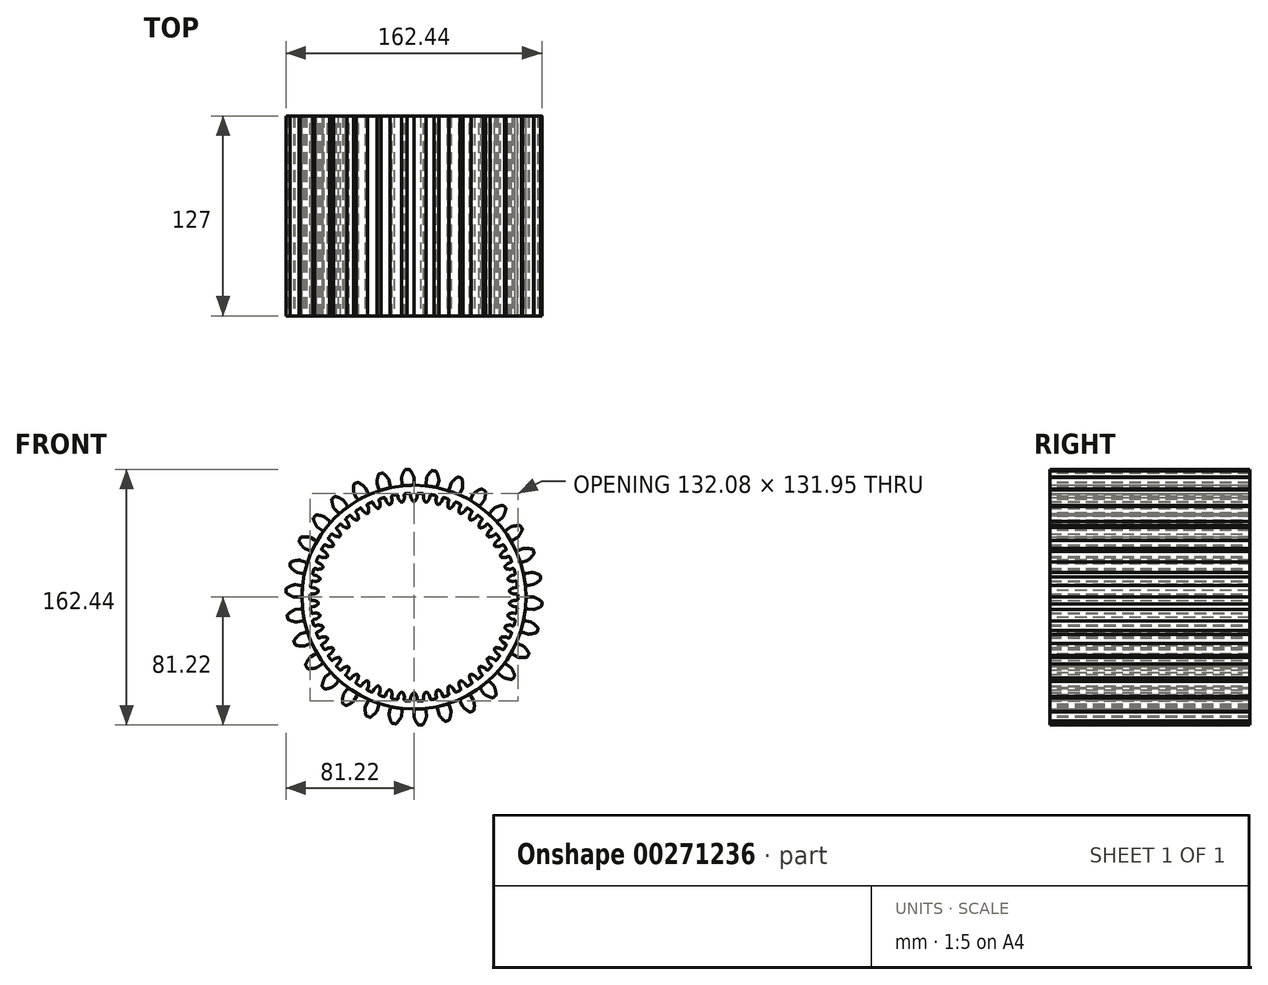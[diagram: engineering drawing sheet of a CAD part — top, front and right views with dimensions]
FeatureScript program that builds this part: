
annotation { "Feature Type Name" : "Feature", "Feature Type Description" : "" }
export const myFeature = defineFeature(function(context is Context, id is Id, definition is map)
    precondition{}
    {
        {
            var Q0;
            Q0=qCreatedBy(makeId("Front.planeOp"),FACE);
            var sketch = newSketch(context, id + "F0", { "sketchPlane" : qUnion([Q0])});
            skArc(sketch, "E0", {"start": v(-2.9, 65.98) * mm, "mid": v(-4.15, 65.9) * mm, "end": v(-5.38, 65.82) * mm});
            skArc(sketch, "E1.MirrorCS", {"start": v(1.94, 63.33) * mm, "mid": v(1.43, 62.22) * mm, "end": v(0.84, 61.15) * mm});
            skLineSegment(sketch, "E2", {"start": v(2, 63.62) * mm, "end": v(2.05, 65.18) * mm});
            skLineSegment(sketch, "E3", {"start": v(0.4, 60.9) * mm, "end": v(0, 60.9) * mm});
            skLineSegment(sketch, "E4.MirrorCS", {"start": v(-2, 63.62) * mm, "end": v(-2.05, 65.18) * mm});
            skArc(sketch, "E5.MirrorCS", {"start": v(-1.94, 63.33) * mm, "mid": v(-1.43, 62.22) * mm, "end": v(-0.84, 61.15) * mm});
            skLineSegment(sketch, "E6.MirrorCS", {"start": v(-0.4, 60.9) * mm, "end": v(0, 60.9) * mm});
            skPoint(sketch, "E7.visualSharp", {"position": v(2, 63.47) * mm});
            skArc(sketch, "E7.filletArc", {"start": v(1.94, 63.33) * mm, "mid": v(1.98, 63.47) * mm, "end": v(2, 63.62) * mm});
            skPoint(sketch, "E8.visualSharp", {"position": v(-2, 63.47) * mm});
            skArc(sketch, "E8.filletArc", {"start": v(-2, 63.62) * mm, "mid": v(-1.98, 63.47) * mm, "end": v(-1.94, 63.33) * mm});
            skPoint(sketch, "E9.visualSharp", {"position": v(-2.07, 66) * mm});
            skArc(sketch, "E9.filletArc", {"start": v(-2.05, 65.18) * mm, "mid": v(-2.31, 65.76) * mm, "end": v(-2.9, 65.98) * mm});
            skPoint(sketch, "E10.visualSharp", {"position": v(2.07, 66) * mm});
            skArc(sketch, "E10.filletArc", {"start": v(2.9, 65.98) * mm, "mid": v(2.31, 65.76) * mm, "end": v(2.05, 65.18) * mm});
            skPoint(sketch, "E11.visualSharp", {"position": v(-0.68, 60.9) * mm});
            skArc(sketch, "E11.filletArc", {"start": v(-0.84, 61.15) * mm, "mid": v(-0.65, 60.97) * mm, "end": v(-0.4, 60.9) * mm});
            skPoint(sketch, "E12.visualSharp", {"position": v(0.68, 60.9) * mm});
            skArc(sketch, "E12.filletArc", {"start": v(0.4, 60.9) * mm, "mid": v(0.65, 60.97) * mm, "end": v(0.84, 61.15) * mm});
            skArc(sketch, "E13.1.0", {"start": v(-5.38, 65.82) * mm, "mid": v(-5.95, 65.53) * mm, "end": v(-6.14, 64.92) * mm});
            skLineSegment(sketch, "E13.1.1", {"start": v(-5.99, 63.37) * mm, "end": v(-6.14, 64.92) * mm});
            skArc(sketch, "E13.1.2", {"start": v(-6.01, 63.07) * mm, "mid": v(-5.99, 63.22) * mm, "end": v(-5.99, 63.37) * mm});
            skArc(sketch, "E13.1.3", {"start": v(-6.01, 63.07) * mm, "mid": v(-6.38, 61.9) * mm, "end": v(-6.83, 60.77) * mm});
            skArc(sketch, "E13.1.4", {"start": v(-7.24, 60.47) * mm, "mid": v(-7, 60.57) * mm, "end": v(-6.83, 60.77) * mm});
            skLineSegment(sketch, "E13.1.5", {"start": v(-7.24, 60.47) * mm, "end": v(-7.63, 60.42) * mm});
            skLineSegment(sketch, "E13.1.6", {"start": v(-8.03, 60.37) * mm, "end": v(-7.63, 60.42) * mm});
            skArc(sketch, "E13.1.7", {"start": v(-8.5, 60.56) * mm, "mid": v(-8.29, 60.4) * mm, "end": v(-8.03, 60.37) * mm});
            skArc(sketch, "E13.1.8", {"start": v(-9.86, 62.59) * mm, "mid": v(-9.21, 61.55) * mm, "end": v(-8.5, 60.56) * mm});
            skPoint(sketch, "E13.1.9", {"position": v(-9.93, 62.72) * mm});
            skArc(sketch, "E13.1.10", {"start": v(-9.96, 62.86) * mm, "mid": v(-9.92, 62.72) * mm, "end": v(-9.86, 62.59) * mm});
            skLineSegment(sketch, "E13.1.11", {"start": v(-9.96, 62.86) * mm, "end": v(-10.2, 64.4) * mm});
            skArc(sketch, "E13.1.12", {"start": v(-10.2, 64.4) * mm, "mid": v(-10.54, 64.95) * mm, "end": v(-11.16, 65.1) * mm});
            skArc(sketch, "E13.2.0", {"start": v(-13.59, 64.63) * mm, "mid": v(-14.11, 64.27) * mm, "end": v(-14.22, 63.64) * mm});
            skLineSegment(sketch, "E13.2.1", {"start": v(-13.88, 62.11) * mm, "end": v(-14.22, 63.64) * mm});
            skArc(sketch, "E13.2.2", {"start": v(-13.87, 61.82) * mm, "mid": v(-13.87, 61.97) * mm, "end": v(-13.88, 62.11) * mm});
            skArc(sketch, "E13.2.3", {"start": v(-13.87, 61.82) * mm, "mid": v(-14.09, 60.62) * mm, "end": v(-14.4, 59.43) * mm});
            skArc(sketch, "E13.2.4", {"start": v(-14.76, 59.09) * mm, "mid": v(-14.53, 59.21) * mm, "end": v(-14.4, 59.43) * mm});
            skLineSegment(sketch, "E13.2.5", {"start": v(-14.76, 59.09) * mm, "end": v(-15.15, 58.99) * mm});
            skLineSegment(sketch, "E13.2.6", {"start": v(-15.53, 58.89) * mm, "end": v(-15.15, 58.99) * mm});
            skArc(sketch, "E13.2.7", {"start": v(-16.02, 59.02) * mm, "mid": v(-15.8, 58.89) * mm, "end": v(-15.53, 58.89) * mm});
            skArc(sketch, "E13.2.8", {"start": v(-17.63, 60.86) * mm, "mid": v(-16.86, 59.9) * mm, "end": v(-16.02, 59.02) * mm});
            skPoint(sketch, "E13.2.9", {"position": v(-17.72, 60.98) * mm});
            skArc(sketch, "E13.2.10", {"start": v(-17.76, 61.12) * mm, "mid": v(-17.7, 60.98) * mm, "end": v(-17.63, 60.86) * mm});
            skLineSegment(sketch, "E13.2.11", {"start": v(-17.76, 61.12) * mm, "end": v(-18.2, 62.62) * mm});
            skArc(sketch, "E13.2.12", {"start": v(-18.2, 62.62) * mm, "mid": v(-18.6, 63.12) * mm, "end": v(-19.23, 63.18) * mm});
            skArc(sketch, "E13.3.0", {"start": v(-21.58, 62.41) * mm, "mid": v(-22.06, 61.99) * mm, "end": v(-22.09, 61.35) * mm});
            skLineSegment(sketch, "E13.3.1", {"start": v(-21.56, 59.88) * mm, "end": v(-22.09, 61.35) * mm});
            skArc(sketch, "E13.3.2", {"start": v(-21.51, 59.6) * mm, "mid": v(-21.52, 59.74) * mm, "end": v(-21.56, 59.88) * mm});
            skArc(sketch, "E13.3.3", {"start": v(-21.51, 59.6) * mm, "mid": v(-21.57, 58.37) * mm, "end": v(-21.73, 57.16) * mm});
            skArc(sketch, "E13.3.4", {"start": v(-22.05, 56.77) * mm, "mid": v(-21.84, 56.92) * mm, "end": v(-21.73, 57.16) * mm});
            skLineSegment(sketch, "E13.3.5", {"start": v(-22.05, 56.77) * mm, "end": v(-22.42, 56.62) * mm});
            skLineSegment(sketch, "E13.3.6", {"start": v(-22.8, 56.48) * mm, "end": v(-22.42, 56.62) * mm});
            skArc(sketch, "E13.3.7", {"start": v(-23.29, 56.54) * mm, "mid": v(-23.05, 56.45) * mm, "end": v(-22.8, 56.48) * mm});
            skArc(sketch, "E13.3.8", {"start": v(-25.11, 58.17) * mm, "mid": v(-24.23, 57.32) * mm, "end": v(-23.29, 56.54) * mm});
            skPoint(sketch, "E13.3.9", {"position": v(-25.22, 58.28) * mm});
            skArc(sketch, "E13.3.10", {"start": v(-25.28, 58.41) * mm, "mid": v(-25.2, 58.28) * mm, "end": v(-25.11, 58.17) * mm});
            skLineSegment(sketch, "E13.3.11", {"start": v(-25.28, 58.41) * mm, "end": v(-25.9, 59.85) * mm});
            skArc(sketch, "E13.3.12", {"start": v(-25.9, 59.85) * mm, "mid": v(-26.36, 60.29) * mm, "end": v(-27, 60.27) * mm});
            skArc(sketch, "E13.4.0", {"start": v(-29.23, 59.22) * mm, "mid": v(-29.65, 58.74) * mm, "end": v(-29.6, 58.1) * mm});
            skLineSegment(sketch, "E13.4.1", {"start": v(-28.9, 56.71) * mm, "end": v(-29.6, 58.1) * mm});
            skArc(sketch, "E13.4.2", {"start": v(-28.81, 56.43) * mm, "mid": v(-28.84, 56.57) * mm, "end": v(-28.9, 56.71) * mm});
            skArc(sketch, "E13.4.3", {"start": v(-28.81, 56.43) * mm, "mid": v(-28.72, 55.2) * mm, "end": v(-28.73, 53.98) * mm});
            skArc(sketch, "E13.4.4", {"start": v(-28.99, 53.56) * mm, "mid": v(-28.8, 53.74) * mm, "end": v(-28.73, 53.98) * mm});
            skLineSegment(sketch, "E13.4.5", {"start": v(-28.99, 53.56) * mm, "end": v(-29.34, 53.37) * mm});
            skLineSegment(sketch, "E13.4.6", {"start": v(-29.7, 53.17) * mm, "end": v(-29.34, 53.37) * mm});
            skArc(sketch, "E13.4.7", {"start": v(-30.19, 53.18) * mm, "mid": v(-29.94, 53.11) * mm, "end": v(-29.7, 53.17) * mm});
            skArc(sketch, "E13.4.8", {"start": v(-32.2, 54.56) * mm, "mid": v(-31.22, 53.83) * mm, "end": v(-30.19, 53.18) * mm});
            skPoint(sketch, "E13.4.9", {"position": v(-32.32, 54.66) * mm});
            skArc(sketch, "E13.4.10", {"start": v(-32.4, 54.78) * mm, "mid": v(-32.31, 54.66) * mm, "end": v(-32.2, 54.56) * mm});
            skLineSegment(sketch, "E13.4.11", {"start": v(-32.4, 54.78) * mm, "end": v(-33.2, 56.13) * mm});
            skArc(sketch, "E13.4.12", {"start": v(-33.2, 56.13) * mm, "mid": v(-33.7, 56.5) * mm, "end": v(-34.33, 56.41) * mm});
            skArc(sketch, "E13.5.0", {"start": v(-36.43, 55.09) * mm, "mid": v(-36.78, 54.56) * mm, "end": v(-36.65, 53.93) * mm});
            skLineSegment(sketch, "E13.5.1", {"start": v(-35.78, 52.64) * mm, "end": v(-36.65, 53.93) * mm});
            skArc(sketch, "E13.5.2", {"start": v(-35.66, 52.37) * mm, "mid": v(-35.7, 52.51) * mm, "end": v(-35.78, 52.64) * mm});
            skArc(sketch, "E13.5.3", {"start": v(-35.66, 52.37) * mm, "mid": v(-35.41, 51.17) * mm, "end": v(-35.26, 49.96) * mm});
            skArc(sketch, "E13.5.4", {"start": v(-35.47, 49.5) * mm, "mid": v(-35.3, 49.7) * mm, "end": v(-35.26, 49.96) * mm});
            skLineSegment(sketch, "E13.5.5", {"start": v(-35.47, 49.5) * mm, "end": v(-35.8, 49.27) * mm});
            skLineSegment(sketch, "E13.5.6", {"start": v(-36.12, 49.03) * mm, "end": v(-35.8, 49.27) * mm});
            skArc(sketch, "E13.5.7", {"start": v(-36.62, 48.98) * mm, "mid": v(-36.36, 48.94) * mm, "end": v(-36.12, 49.03) * mm});
            skArc(sketch, "E13.5.8", {"start": v(-38.8, 50.1) * mm, "mid": v(-37.73, 49.5) * mm, "end": v(-36.62, 48.98) * mm});
            skPoint(sketch, "E13.5.9", {"position": v(-38.92, 50.17) * mm});
            skArc(sketch, "E13.5.10", {"start": v(-39.01, 50.3) * mm, "mid": v(-38.9, 50.18) * mm, "end": v(-38.8, 50.1) * mm});
            skLineSegment(sketch, "E13.5.11", {"start": v(-39.01, 50.3) * mm, "end": v(-39.97, 51.53) * mm});
            skArc(sketch, "E13.5.12", {"start": v(-39.97, 51.53) * mm, "mid": v(-40.52, 51.84) * mm, "end": v(-41.13, 51.67) * mm});
            skArc(sketch, "E13.6.0", {"start": v(-43.04, 50.09) * mm, "mid": v(-43.33, 49.52) * mm, "end": v(-43.12, 48.91) * mm});
            skLineSegment(sketch, "E13.6.1", {"start": v(-42.1, 47.74) * mm, "end": v(-43.12, 48.91) * mm});
            skArc(sketch, "E13.6.2", {"start": v(-41.94, 47.5) * mm, "mid": v(-42, 47.62) * mm, "end": v(-42.1, 47.74) * mm});
            skArc(sketch, "E13.6.3", {"start": v(-41.94, 47.5) * mm, "mid": v(-41.55, 46.33) * mm, "end": v(-41.25, 45.15) * mm});
            skArc(sketch, "E13.6.4", {"start": v(-41.4, 44.67) * mm, "mid": v(-41.26, 44.89) * mm, "end": v(-41.25, 45.15) * mm});
            skLineSegment(sketch, "E13.6.5", {"start": v(-41.4, 44.67) * mm, "end": v(-41.69, 44.4) * mm});
            skLineSegment(sketch, "E13.6.6", {"start": v(-41.98, 44.12) * mm, "end": v(-41.69, 44.4) * mm});
            skArc(sketch, "E13.6.7", {"start": v(-42.47, 44) * mm, "mid": v(-42.2, 44) * mm, "end": v(-41.98, 44.12) * mm});
            skArc(sketch, "E13.6.8", {"start": v(-44.76, 44.84) * mm, "mid": v(-43.63, 44.38) * mm, "end": v(-42.47, 44) * mm});
            skPoint(sketch, "E13.6.9", {"position": v(-44.9, 44.9) * mm});
            skArc(sketch, "E13.6.10", {"start": v(-45, 45) * mm, "mid": v(-44.9, 44.91) * mm, "end": v(-44.76, 44.84) * mm});
            skLineSegment(sketch, "E13.6.11", {"start": v(-45, 45) * mm, "end": v(-46.1, 46.1) * mm});
            skArc(sketch, "E13.6.12", {"start": v(-46.1, 46.1) * mm, "mid": v(-46.7, 46.35) * mm, "end": v(-47.28, 46.1) * mm});
            skArc(sketch, "E13.7.0", {"start": v(-48.98, 44.3) * mm, "mid": v(-49.2, 43.7) * mm, "end": v(-48.91, 43.12) * mm});
            skLineSegment(sketch, "E13.7.1", {"start": v(-47.74, 42.1) * mm, "end": v(-48.91, 43.12) * mm});
            skArc(sketch, "E13.7.2", {"start": v(-47.56, 41.86) * mm, "mid": v(-47.64, 41.98) * mm, "end": v(-47.74, 42.1) * mm});
            skArc(sketch, "E13.7.3", {"start": v(-47.56, 41.86) * mm, "mid": v(-47.03, 40.76) * mm, "end": v(-46.58, 39.62) * mm});
            skArc(sketch, "E13.7.4", {"start": v(-46.67, 39.13) * mm, "mid": v(-46.56, 39.36) * mm, "end": v(-46.58, 39.62) * mm});
            skLineSegment(sketch, "E13.7.5", {"start": v(-46.67, 39.13) * mm, "end": v(-46.92, 38.82) * mm});
            skLineSegment(sketch, "E13.7.6", {"start": v(-47.18, 38.51) * mm, "end": v(-46.92, 38.82) * mm});
            skArc(sketch, "E13.7.7", {"start": v(-47.65, 38.33) * mm, "mid": v(-47.39, 38.36) * mm, "end": v(-47.18, 38.51) * mm});
            skArc(sketch, "E13.7.8", {"start": v(-50.03, 38.87) * mm, "mid": v(-48.85, 38.56) * mm, "end": v(-47.65, 38.33) * mm});
            skPoint(sketch, "E13.7.9", {"position": v(-50.17, 38.92) * mm});
            skArc(sketch, "E13.7.10", {"start": v(-50.3, 39.01) * mm, "mid": v(-50.17, 38.93) * mm, "end": v(-50.03, 38.87) * mm});
            skLineSegment(sketch, "E13.7.11", {"start": v(-50.3, 39.01) * mm, "end": v(-51.53, 39.97) * mm});
            skArc(sketch, "E13.7.12", {"start": v(-51.53, 39.97) * mm, "mid": v(-52.14, 40.13) * mm, "end": v(-52.7, 39.81) * mm});
            skArc(sketch, "E13.8.0", {"start": v(-54.15, 37.8) * mm, "mid": v(-54.28, 37.19) * mm, "end": v(-53.93, 36.65) * mm});
            skLineSegment(sketch, "E13.8.1", {"start": v(-52.64, 35.78) * mm, "end": v(-53.93, 36.65) * mm});
            skArc(sketch, "E13.8.2", {"start": v(-52.43, 35.57) * mm, "mid": v(-52.53, 35.68) * mm, "end": v(-52.64, 35.78) * mm});
            skArc(sketch, "E13.8.3", {"start": v(-52.43, 35.57) * mm, "mid": v(-51.76, 34.54) * mm, "end": v(-51.18, 33.47) * mm});
            skArc(sketch, "E13.8.4", {"start": v(-51.2, 32.97) * mm, "mid": v(-51.13, 33.22) * mm, "end": v(-51.18, 33.47) * mm});
            skLineSegment(sketch, "E13.8.5", {"start": v(-51.2, 32.97) * mm, "end": v(-51.42, 32.63) * mm});
            skLineSegment(sketch, "E13.8.6", {"start": v(-51.64, 32.3) * mm, "end": v(-51.42, 32.63) * mm});
            skArc(sketch, "E13.8.7", {"start": v(-52.07, 32.06) * mm, "mid": v(-51.82, 32.12) * mm, "end": v(-51.64, 32.3) * mm});
            skArc(sketch, "E13.8.8", {"start": v(-54.5, 32.3) * mm, "mid": v(-53.3, 32.13) * mm, "end": v(-52.07, 32.06) * mm});
            skPoint(sketch, "E13.8.9", {"position": v(-54.66, 32.32) * mm});
            skArc(sketch, "E13.8.10", {"start": v(-54.78, 32.4) * mm, "mid": v(-54.65, 32.34) * mm, "end": v(-54.5, 32.3) * mm});
            skLineSegment(sketch, "E13.8.11", {"start": v(-54.78, 32.4) * mm, "end": v(-56.13, 33.2) * mm});
            skArc(sketch, "E13.8.12", {"start": v(-56.13, 33.2) * mm, "mid": v(-56.76, 33.28) * mm, "end": v(-57.26, 32.9) * mm});
            skArc(sketch, "E13.9.0", {"start": v(-58.46, 30.72) * mm, "mid": v(-58.51, 30.09) * mm, "end": v(-58.1, 29.6) * mm});
            skLineSegment(sketch, "E13.9.1", {"start": v(-56.71, 28.9) * mm, "end": v(-58.1, 29.6) * mm});
            skArc(sketch, "E13.9.2", {"start": v(-56.48, 28.72) * mm, "mid": v(-56.59, 28.82) * mm, "end": v(-56.71, 28.9) * mm});
            skArc(sketch, "E13.9.3", {"start": v(-56.48, 28.72) * mm, "mid": v(-55.69, 27.78) * mm, "end": v(-54.97, 26.8) * mm});
            skArc(sketch, "E13.9.4", {"start": v(-54.93, 26.3) * mm, "mid": v(-54.89, 26.55) * mm, "end": v(-54.97, 26.8) * mm});
            skLineSegment(sketch, "E13.9.5", {"start": v(-54.93, 26.3) * mm, "end": v(-55.1, 25.93) * mm});
            skLineSegment(sketch, "E13.9.6", {"start": v(-55.28, 25.57) * mm, "end": v(-55.1, 25.93) * mm});
            skArc(sketch, "E13.9.7", {"start": v(-55.68, 25.28) * mm, "mid": v(-55.44, 25.37) * mm, "end": v(-55.28, 25.57) * mm});
            skArc(sketch, "E13.9.8", {"start": v(-58.13, 25.21) * mm, "mid": v(-56.9, 25.2) * mm, "end": v(-55.68, 25.28) * mm});
            skPoint(sketch, "E13.9.9", {"position": v(-58.28, 25.22) * mm});
            skArc(sketch, "E13.9.10", {"start": v(-58.41, 25.28) * mm, "mid": v(-58.27, 25.23) * mm, "end": v(-58.13, 25.21) * mm});
            skLineSegment(sketch, "E13.9.11", {"start": v(-58.41, 25.28) * mm, "end": v(-59.85, 25.9) * mm});
            skArc(sketch, "E13.9.12", {"start": v(-59.85, 25.9) * mm, "mid": v(-60.48, 25.9) * mm, "end": v(-60.94, 25.46) * mm});
            skArc(sketch, "E13.10.0", {"start": v(-61.85, 23.15) * mm, "mid": v(-61.82, 22.52) * mm, "end": v(-61.35, 22.09) * mm});
            skLineSegment(sketch, "E13.10.1", {"start": v(-59.88, 21.56) * mm, "end": v(-61.35, 22.09) * mm});
            skArc(sketch, "E13.10.2", {"start": v(-59.63, 21.41) * mm, "mid": v(-59.75, 21.5) * mm, "end": v(-59.88, 21.56) * mm});
            skArc(sketch, "E13.10.3", {"start": v(-59.63, 21.41) * mm, "mid": v(-58.73, 20.58) * mm, "end": v(-57.9, 19.69) * mm});
            skArc(sketch, "E13.10.4", {"start": v(-57.8, 19.2) * mm, "mid": v(-57.78, 19.46) * mm, "end": v(-57.9, 19.69) * mm});
            skLineSegment(sketch, "E13.10.5", {"start": v(-57.8, 19.2) * mm, "end": v(-57.92, 18.82) * mm});
            skLineSegment(sketch, "E13.10.6", {"start": v(-58.04, 18.44) * mm, "end": v(-57.92, 18.82) * mm});
            skArc(sketch, "E13.10.7", {"start": v(-58.41, 18.1) * mm, "mid": v(-58.18, 18.22) * mm, "end": v(-58.04, 18.44) * mm});
            skArc(sketch, "E13.10.8", {"start": v(-60.83, 17.73) * mm, "mid": v(-59.61, 17.87) * mm, "end": v(-58.41, 18.1) * mm});
            skPoint(sketch, "E13.10.9", {"position": v(-60.98, 17.72) * mm});
            skArc(sketch, "E13.10.10", {"start": v(-61.12, 17.76) * mm, "mid": v(-60.98, 17.73) * mm, "end": v(-60.83, 17.73) * mm});
            skLineSegment(sketch, "E13.10.11", {"start": v(-61.12, 17.76) * mm, "end": v(-62.62, 18.2) * mm});
            skArc(sketch, "E13.10.12", {"start": v(-62.62, 18.2) * mm, "mid": v(-63.25, 18.12) * mm, "end": v(-63.65, 17.62) * mm});
            skArc(sketch, "E13.11.0", {"start": v(-64.26, 15.22) * mm, "mid": v(-64.16, 14.6) * mm, "end": v(-63.64, 14.22) * mm});
            skLineSegment(sketch, "E13.11.1", {"start": v(-62.11, 13.88) * mm, "end": v(-63.64, 14.22) * mm});
            skArc(sketch, "E13.11.2", {"start": v(-61.84, 13.77) * mm, "mid": v(-61.97, 13.84) * mm, "end": v(-62.11, 13.88) * mm});
            skArc(sketch, "E13.11.3", {"start": v(-61.84, 13.77) * mm, "mid": v(-60.85, 13.06) * mm, "end": v(-59.9, 12.28) * mm});
            skArc(sketch, "E13.11.4", {"start": v(-59.75, 11.8) * mm, "mid": v(-59.76, 12.06) * mm, "end": v(-59.9, 12.28) * mm});
            skLineSegment(sketch, "E13.11.5", {"start": v(-59.75, 11.8) * mm, "end": v(-59.82, 11.41) * mm});
            skLineSegment(sketch, "E13.11.6", {"start": v(-59.9, 11.02) * mm, "end": v(-59.82, 11.41) * mm});
            skArc(sketch, "E13.11.7", {"start": v(-60.22, 10.64) * mm, "mid": v(-60, 10.79) * mm, "end": v(-59.9, 11.02) * mm});
            skArc(sketch, "E13.11.8", {"start": v(-62.57, 9.96) * mm, "mid": v(-61.38, 10.25) * mm, "end": v(-60.22, 10.64) * mm});
            skPoint(sketch, "E13.11.9", {"position": v(-62.72, 9.93) * mm});
            skArc(sketch, "E13.11.10", {"start": v(-62.86, 9.96) * mm, "mid": v(-62.72, 9.95) * mm, "end": v(-62.57, 9.96) * mm});
            skLineSegment(sketch, "E13.11.11", {"start": v(-62.86, 9.96) * mm, "end": v(-64.4, 10.2) * mm});
            skArc(sketch, "E13.11.12", {"start": v(-64.4, 10.2) * mm, "mid": v(-65.03, 10.05) * mm, "end": v(-65.35, 9.5) * mm});
            skArc(sketch, "E13.12.0", {"start": v(-65.66, 7.05) * mm, "mid": v(-65.48, 6.44) * mm, "end": v(-64.92, 6.14) * mm});
            skLineSegment(sketch, "E13.12.1", {"start": v(-63.37, 5.99) * mm, "end": v(-64.92, 6.14) * mm});
            skArc(sketch, "E13.12.2", {"start": v(-63.08, 5.91) * mm, "mid": v(-63.22, 5.96) * mm, "end": v(-63.37, 5.99) * mm});
            skArc(sketch, "E13.12.3", {"start": v(-63.08, 5.91) * mm, "mid": v(-62, 5.33) * mm, "end": v(-60.97, 4.67) * mm});
            skArc(sketch, "E13.12.4", {"start": v(-60.76, 4.22) * mm, "mid": v(-60.8, 4.48) * mm, "end": v(-60.97, 4.67) * mm});
            skLineSegment(sketch, "E13.12.5", {"start": v(-60.76, 4.22) * mm, "end": v(-60.78, 3.82) * mm});
            skLineSegment(sketch, "E13.12.6", {"start": v(-60.8, 3.42) * mm, "end": v(-60.78, 3.82) * mm});
            skArc(sketch, "E13.12.7", {"start": v(-61.08, 3) * mm, "mid": v(-60.89, 3.18) * mm, "end": v(-60.8, 3.42) * mm});
            skArc(sketch, "E13.12.8", {"start": v(-63.32, 2.04) * mm, "mid": v(-62.18, 2.48) * mm, "end": v(-61.08, 3) * mm});
            skPoint(sketch, "E13.12.9", {"position": v(-63.47, 2) * mm});
            skArc(sketch, "E13.12.10", {"start": v(-63.62, 2) * mm, "mid": v(-63.47, 2) * mm, "end": v(-63.32, 2.04) * mm});
            skLineSegment(sketch, "E13.12.11", {"start": v(-63.62, 2) * mm, "end": v(-65.18, 2.05) * mm});
            skArc(sketch, "E13.12.12", {"start": v(-65.18, 2.05) * mm, "mid": v(-65.77, 1.82) * mm, "end": v(-66.03, 1.24) * mm});
            skArc(sketch, "E13.13.0", {"start": v(-66.03, -1.24) * mm, "mid": v(-65.77, -1.82) * mm, "end": v(-65.18, -2.05) * mm});
            skLineSegment(sketch, "E13.13.1", {"start": v(-63.62, -2) * mm, "end": v(-65.18, -2.05) * mm});
            skArc(sketch, "E13.13.2", {"start": v(-63.32, -2.04) * mm, "mid": v(-63.47, -2) * mm, "end": v(-63.62, -2) * mm});
            skArc(sketch, "E13.13.3", {"start": v(-63.32, -2.04) * mm, "mid": v(-62.18, -2.48) * mm, "end": v(-61.08, -3) * mm});
            skArc(sketch, "E13.13.4", {"start": v(-60.8, -3.42) * mm, "mid": v(-60.89, -3.18) * mm, "end": v(-61.08, -3) * mm});
            skLineSegment(sketch, "E13.13.5", {"start": v(-60.8, -3.42) * mm, "end": v(-60.78, -3.82) * mm});
            skLineSegment(sketch, "E13.13.6", {"start": v(-60.76, -4.22) * mm, "end": v(-60.78, -3.82) * mm});
            skArc(sketch, "E13.13.7", {"start": v(-60.97, -4.67) * mm, "mid": v(-60.8, -4.48) * mm, "end": v(-60.76, -4.22) * mm});
            skArc(sketch, "E13.13.8", {"start": v(-63.08, -5.91) * mm, "mid": v(-62, -5.33) * mm, "end": v(-60.97, -4.67) * mm});
            skPoint(sketch, "E13.13.9", {"position": v(-63.22, -5.98) * mm});
            skArc(sketch, "E13.13.10", {"start": v(-63.37, -5.99) * mm, "mid": v(-63.22, -5.96) * mm, "end": v(-63.08, -5.91) * mm});
            skLineSegment(sketch, "E13.13.11", {"start": v(-63.37, -5.99) * mm, "end": v(-64.92, -6.14) * mm});
            skArc(sketch, "E13.13.12", {"start": v(-64.92, -6.14) * mm, "mid": v(-65.48, -6.44) * mm, "end": v(-65.66, -7.05) * mm});
            skArc(sketch, "E13.14.0", {"start": v(-65.35, -9.5) * mm, "mid": v(-65.03, -10.05) * mm, "end": v(-64.4, -10.2) * mm});
            skLineSegment(sketch, "E13.14.1", {"start": v(-62.86, -9.96) * mm, "end": v(-64.4, -10.2) * mm});
            skArc(sketch, "E13.14.2", {"start": v(-62.57, -9.96) * mm, "mid": v(-62.72, -9.95) * mm, "end": v(-62.86, -9.96) * mm});
            skArc(sketch, "E13.14.3", {"start": v(-62.57, -9.96) * mm, "mid": v(-61.38, -10.25) * mm, "end": v(-60.22, -10.64) * mm});
            skArc(sketch, "E13.14.4", {"start": v(-59.9, -11.02) * mm, "mid": v(-60, -10.79) * mm, "end": v(-60.22, -10.64) * mm});
            skLineSegment(sketch, "E13.14.5", {"start": v(-59.9, -11.02) * mm, "end": v(-59.82, -11.41) * mm});
            skLineSegment(sketch, "E13.14.6", {"start": v(-59.75, -11.8) * mm, "end": v(-59.82, -11.41) * mm});
            skArc(sketch, "E13.14.7", {"start": v(-59.9, -12.28) * mm, "mid": v(-59.76, -12.06) * mm, "end": v(-59.75, -11.8) * mm});
            skArc(sketch, "E13.14.8", {"start": v(-61.84, -13.77) * mm, "mid": v(-60.85, -13.06) * mm, "end": v(-59.9, -12.28) * mm});
            skPoint(sketch, "E13.14.9", {"position": v(-61.97, -13.85) * mm});
            skArc(sketch, "E13.14.10", {"start": v(-62.11, -13.88) * mm, "mid": v(-61.97, -13.84) * mm, "end": v(-61.84, -13.77) * mm});
            skLineSegment(sketch, "E13.14.11", {"start": v(-62.11, -13.88) * mm, "end": v(-63.64, -14.22) * mm});
            skArc(sketch, "E13.14.12", {"start": v(-63.64, -14.22) * mm, "mid": v(-64.16, -14.6) * mm, "end": v(-64.26, -15.22) * mm});
            skArc(sketch, "E13.15.0", {"start": v(-63.65, -17.62) * mm, "mid": v(-63.25, -18.12) * mm, "end": v(-62.62, -18.2) * mm});
            skLineSegment(sketch, "E13.15.1", {"start": v(-61.12, -17.76) * mm, "end": v(-62.62, -18.2) * mm});
            skArc(sketch, "E13.15.2", {"start": v(-60.83, -17.73) * mm, "mid": v(-60.98, -17.73) * mm, "end": v(-61.12, -17.76) * mm});
            skArc(sketch, "E13.15.3", {"start": v(-60.83, -17.73) * mm, "mid": v(-59.61, -17.87) * mm, "end": v(-58.41, -18.1) * mm});
            skArc(sketch, "E13.15.4", {"start": v(-58.04, -18.44) * mm, "mid": v(-58.18, -18.22) * mm, "end": v(-58.41, -18.1) * mm});
            skLineSegment(sketch, "E13.15.5", {"start": v(-58.04, -18.44) * mm, "end": v(-57.92, -18.82) * mm});
            skLineSegment(sketch, "E13.15.6", {"start": v(-57.8, -19.2) * mm, "end": v(-57.92, -18.82) * mm});
            skArc(sketch, "E13.15.7", {"start": v(-57.9, -19.69) * mm, "mid": v(-57.78, -19.46) * mm, "end": v(-57.8, -19.2) * mm});
            skArc(sketch, "E13.15.8", {"start": v(-59.63, -21.41) * mm, "mid": v(-58.73, -20.58) * mm, "end": v(-57.9, -19.69) * mm});
            skPoint(sketch, "E13.15.9", {"position": v(-59.75, -21.5) * mm});
            skArc(sketch, "E13.15.10", {"start": v(-59.88, -21.56) * mm, "mid": v(-59.75, -21.5) * mm, "end": v(-59.63, -21.41) * mm});
            skLineSegment(sketch, "E13.15.11", {"start": v(-59.88, -21.56) * mm, "end": v(-61.35, -22.09) * mm});
            skArc(sketch, "E13.15.12", {"start": v(-61.35, -22.09) * mm, "mid": v(-61.82, -22.52) * mm, "end": v(-61.85, -23.15) * mm});
            skArc(sketch, "E13.16.0", {"start": v(-60.94, -25.46) * mm, "mid": v(-60.48, -25.9) * mm, "end": v(-59.85, -25.9) * mm});
            skLineSegment(sketch, "E13.16.1", {"start": v(-58.41, -25.28) * mm, "end": v(-59.85, -25.9) * mm});
            skArc(sketch, "E13.16.2", {"start": v(-58.13, -25.21) * mm, "mid": v(-58.27, -25.23) * mm, "end": v(-58.41, -25.28) * mm});
            skArc(sketch, "E13.16.3", {"start": v(-58.13, -25.21) * mm, "mid": v(-56.9, -25.2) * mm, "end": v(-55.68, -25.28) * mm});
            skArc(sketch, "E13.16.4", {"start": v(-55.28, -25.57) * mm, "mid": v(-55.44, -25.37) * mm, "end": v(-55.68, -25.28) * mm});
            skLineSegment(sketch, "E13.16.5", {"start": v(-55.28, -25.57) * mm, "end": v(-55.1, -25.93) * mm});
            skLineSegment(sketch, "E13.16.6", {"start": v(-54.93, -26.3) * mm, "end": v(-55.1, -25.93) * mm});
            skArc(sketch, "E13.16.7", {"start": v(-54.97, -26.8) * mm, "mid": v(-54.89, -26.55) * mm, "end": v(-54.93, -26.3) * mm});
            skArc(sketch, "E13.16.8", {"start": v(-56.48, -28.72) * mm, "mid": v(-55.69, -27.78) * mm, "end": v(-54.97, -26.8) * mm});
            skPoint(sketch, "E13.16.9", {"position": v(-56.58, -28.83) * mm});
            skArc(sketch, "E13.16.10", {"start": v(-56.71, -28.9) * mm, "mid": v(-56.59, -28.82) * mm, "end": v(-56.48, -28.72) * mm});
            skLineSegment(sketch, "E13.16.11", {"start": v(-56.71, -28.9) * mm, "end": v(-58.1, -29.6) * mm});
            skArc(sketch, "E13.16.12", {"start": v(-58.1, -29.6) * mm, "mid": v(-58.51, -30.09) * mm, "end": v(-58.46, -30.72) * mm});
            skArc(sketch, "E13.17.0", {"start": v(-57.26, -32.9) * mm, "mid": v(-56.76, -33.28) * mm, "end": v(-56.13, -33.2) * mm});
            skLineSegment(sketch, "E13.17.1", {"start": v(-54.78, -32.4) * mm, "end": v(-56.13, -33.2) * mm});
            skArc(sketch, "E13.17.2", {"start": v(-54.5, -32.3) * mm, "mid": v(-54.65, -32.34) * mm, "end": v(-54.78, -32.4) * mm});
            skArc(sketch, "E13.17.3", {"start": v(-54.5, -32.3) * mm, "mid": v(-53.3, -32.13) * mm, "end": v(-52.07, -32.06) * mm});
            skArc(sketch, "E13.17.4", {"start": v(-51.64, -32.3) * mm, "mid": v(-51.82, -32.12) * mm, "end": v(-52.07, -32.06) * mm});
            skLineSegment(sketch, "E13.17.5", {"start": v(-51.64, -32.3) * mm, "end": v(-51.42, -32.63) * mm});
            skLineSegment(sketch, "E13.17.6", {"start": v(-51.2, -32.97) * mm, "end": v(-51.42, -32.63) * mm});
            skArc(sketch, "E13.17.7", {"start": v(-51.18, -33.47) * mm, "mid": v(-51.13, -33.22) * mm, "end": v(-51.2, -32.97) * mm});
            skArc(sketch, "E13.17.8", {"start": v(-52.43, -35.57) * mm, "mid": v(-51.76, -34.54) * mm, "end": v(-51.18, -33.47) * mm});
            skPoint(sketch, "E13.17.9", {"position": v(-52.52, -35.7) * mm});
            skArc(sketch, "E13.17.10", {"start": v(-52.64, -35.78) * mm, "mid": v(-52.53, -35.68) * mm, "end": v(-52.43, -35.57) * mm});
            skLineSegment(sketch, "E13.17.11", {"start": v(-52.64, -35.78) * mm, "end": v(-53.93, -36.65) * mm});
            skArc(sketch, "E13.17.12", {"start": v(-53.93, -36.65) * mm, "mid": v(-54.28, -37.19) * mm, "end": v(-54.15, -37.8) * mm});
            skArc(sketch, "E13.18.0", {"start": v(-52.7, -39.81) * mm, "mid": v(-52.14, -40.13) * mm, "end": v(-51.53, -39.97) * mm});
            skLineSegment(sketch, "E13.18.1", {"start": v(-50.3, -39.01) * mm, "end": v(-51.53, -39.97) * mm});
            skArc(sketch, "E13.18.2", {"start": v(-50.03, -38.87) * mm, "mid": v(-50.17, -38.93) * mm, "end": v(-50.3, -39.01) * mm});
            skArc(sketch, "E13.18.3", {"start": v(-50.03, -38.87) * mm, "mid": v(-48.85, -38.56) * mm, "end": v(-47.65, -38.33) * mm});
            skArc(sketch, "E13.18.4", {"start": v(-47.18, -38.51) * mm, "mid": v(-47.39, -38.36) * mm, "end": v(-47.65, -38.33) * mm});
            skLineSegment(sketch, "E13.18.5", {"start": v(-47.18, -38.51) * mm, "end": v(-46.92, -38.82) * mm});
            skLineSegment(sketch, "E13.18.6", {"start": v(-46.67, -39.13) * mm, "end": v(-46.92, -38.82) * mm});
            skArc(sketch, "E13.18.7", {"start": v(-46.58, -39.62) * mm, "mid": v(-46.56, -39.36) * mm, "end": v(-46.67, -39.13) * mm});
            skArc(sketch, "E13.18.8", {"start": v(-47.56, -41.86) * mm, "mid": v(-47.03, -40.76) * mm, "end": v(-46.58, -39.62) * mm});
            skPoint(sketch, "E13.18.9", {"position": v(-47.63, -42) * mm});
            skArc(sketch, "E13.18.10", {"start": v(-47.74, -42.1) * mm, "mid": v(-47.64, -41.98) * mm, "end": v(-47.56, -41.86) * mm});
            skLineSegment(sketch, "E13.18.11", {"start": v(-47.74, -42.1) * mm, "end": v(-48.91, -43.12) * mm});
            skArc(sketch, "E13.18.12", {"start": v(-48.91, -43.12) * mm, "mid": v(-49.2, -43.7) * mm, "end": v(-48.98, -44.3) * mm});
            skArc(sketch, "E13.19.0", {"start": v(-47.28, -46.1) * mm, "mid": v(-46.7, -46.35) * mm, "end": v(-46.1, -46.1) * mm});
            skLineSegment(sketch, "E13.19.1", {"start": v(-45, -45) * mm, "end": v(-46.1, -46.1) * mm});
            skArc(sketch, "E13.19.2", {"start": v(-44.76, -44.84) * mm, "mid": v(-44.9, -44.91) * mm, "end": v(-45, -45) * mm});
            skArc(sketch, "E13.19.3", {"start": v(-44.76, -44.84) * mm, "mid": v(-43.63, -44.38) * mm, "end": v(-42.47, -44) * mm});
            skArc(sketch, "E13.19.4", {"start": v(-41.98, -44.12) * mm, "mid": v(-42.2, -44) * mm, "end": v(-42.47, -44) * mm});
            skLineSegment(sketch, "E13.19.5", {"start": v(-41.98, -44.12) * mm, "end": v(-41.69, -44.4) * mm});
            skLineSegment(sketch, "E13.19.6", {"start": v(-41.4, -44.67) * mm, "end": v(-41.69, -44.4) * mm});
            skArc(sketch, "E13.19.7", {"start": v(-41.25, -45.15) * mm, "mid": v(-41.26, -44.89) * mm, "end": v(-41.4, -44.67) * mm});
            skArc(sketch, "E13.19.8", {"start": v(-41.94, -47.5) * mm, "mid": v(-41.55, -46.33) * mm, "end": v(-41.25, -45.15) * mm});
            skPoint(sketch, "E13.19.9", {"position": v(-42, -47.63) * mm});
            skArc(sketch, "E13.19.10", {"start": v(-42.1, -47.74) * mm, "mid": v(-42, -47.62) * mm, "end": v(-41.94, -47.5) * mm});
            skLineSegment(sketch, "E13.19.11", {"start": v(-42.1, -47.74) * mm, "end": v(-43.12, -48.91) * mm});
            skArc(sketch, "E13.19.12", {"start": v(-43.12, -48.91) * mm, "mid": v(-43.33, -49.52) * mm, "end": v(-43.04, -50.09) * mm});
            skArc(sketch, "E13.20.0", {"start": v(-41.13, -51.67) * mm, "mid": v(-40.52, -51.84) * mm, "end": v(-39.97, -51.53) * mm});
            skLineSegment(sketch, "E13.20.1", {"start": v(-39.01, -50.3) * mm, "end": v(-39.97, -51.53) * mm});
            skArc(sketch, "E13.20.2", {"start": v(-38.8, -50.1) * mm, "mid": v(-38.9, -50.18) * mm, "end": v(-39.01, -50.3) * mm});
            skArc(sketch, "E13.20.3", {"start": v(-38.8, -50.1) * mm, "mid": v(-37.73, -49.5) * mm, "end": v(-36.62, -48.98) * mm});
            skArc(sketch, "E13.20.4", {"start": v(-36.12, -49.03) * mm, "mid": v(-36.36, -48.94) * mm, "end": v(-36.62, -48.98) * mm});
            skLineSegment(sketch, "E13.20.5", {"start": v(-36.12, -49.03) * mm, "end": v(-35.8, -49.27) * mm});
            skLineSegment(sketch, "E13.20.6", {"start": v(-35.47, -49.5) * mm, "end": v(-35.8, -49.27) * mm});
            skArc(sketch, "E13.20.7", {"start": v(-35.26, -49.96) * mm, "mid": v(-35.3, -49.7) * mm, "end": v(-35.47, -49.5) * mm});
            skArc(sketch, "E13.20.8", {"start": v(-35.66, -52.37) * mm, "mid": v(-35.41, -51.17) * mm, "end": v(-35.26, -49.96) * mm});
            skPoint(sketch, "E13.20.9", {"position": v(-35.7, -52.52) * mm});
            skArc(sketch, "E13.20.10", {"start": v(-35.78, -52.64) * mm, "mid": v(-35.7, -52.51) * mm, "end": v(-35.66, -52.37) * mm});
            skLineSegment(sketch, "E13.20.11", {"start": v(-35.78, -52.64) * mm, "end": v(-36.65, -53.93) * mm});
            skArc(sketch, "E13.20.12", {"start": v(-36.65, -53.93) * mm, "mid": v(-36.78, -54.56) * mm, "end": v(-36.43, -55.09) * mm});
            skArc(sketch, "E13.21.0", {"start": v(-34.33, -56.41) * mm, "mid": v(-33.7, -56.5) * mm, "end": v(-33.2, -56.13) * mm});
            skLineSegment(sketch, "E13.21.1", {"start": v(-32.4, -54.78) * mm, "end": v(-33.2, -56.13) * mm});
            skArc(sketch, "E13.21.2", {"start": v(-32.2, -54.56) * mm, "mid": v(-32.31, -54.66) * mm, "end": v(-32.4, -54.78) * mm});
            skArc(sketch, "E13.21.3", {"start": v(-32.2, -54.56) * mm, "mid": v(-31.22, -53.83) * mm, "end": v(-30.19, -53.18) * mm});
            skArc(sketch, "E13.21.4", {"start": v(-29.7, -53.17) * mm, "mid": v(-29.94, -53.11) * mm, "end": v(-30.19, -53.18) * mm});
            skLineSegment(sketch, "E13.21.5", {"start": v(-29.7, -53.17) * mm, "end": v(-29.34, -53.37) * mm});
            skLineSegment(sketch, "E13.21.6", {"start": v(-28.99, -53.56) * mm, "end": v(-29.34, -53.37) * mm});
            skArc(sketch, "E13.21.7", {"start": v(-28.73, -53.98) * mm, "mid": v(-28.8, -53.74) * mm, "end": v(-28.99, -53.56) * mm});
            skArc(sketch, "E13.21.8", {"start": v(-28.81, -56.43) * mm, "mid": v(-28.72, -55.2) * mm, "end": v(-28.73, -53.98) * mm});
            skPoint(sketch, "E13.21.9", {"position": v(-28.83, -56.58) * mm});
            skArc(sketch, "E13.21.10", {"start": v(-28.9, -56.71) * mm, "mid": v(-28.84, -56.57) * mm, "end": v(-28.81, -56.43) * mm});
            skLineSegment(sketch, "E13.21.11", {"start": v(-28.9, -56.71) * mm, "end": v(-29.6, -58.1) * mm});
            skArc(sketch, "E13.21.12", {"start": v(-29.6, -58.1) * mm, "mid": v(-29.65, -58.74) * mm, "end": v(-29.23, -59.22) * mm});
            skArc(sketch, "E13.22.0", {"start": v(-27, -60.27) * mm, "mid": v(-26.36, -60.29) * mm, "end": v(-25.9, -59.85) * mm});
            skLineSegment(sketch, "E13.22.1", {"start": v(-25.28, -58.41) * mm, "end": v(-25.9, -59.85) * mm});
            skArc(sketch, "E13.22.2", {"start": v(-25.11, -58.17) * mm, "mid": v(-25.2, -58.28) * mm, "end": v(-25.28, -58.41) * mm});
            skArc(sketch, "E13.22.3", {"start": v(-25.11, -58.17) * mm, "mid": v(-24.23, -57.32) * mm, "end": v(-23.29, -56.54) * mm});
            skArc(sketch, "E13.22.4", {"start": v(-22.8, -56.48) * mm, "mid": v(-23.05, -56.45) * mm, "end": v(-23.29, -56.54) * mm});
            skLineSegment(sketch, "E13.22.5", {"start": v(-22.8, -56.48) * mm, "end": v(-22.42, -56.62) * mm});
            skLineSegment(sketch, "E13.22.6", {"start": v(-22.05, -56.77) * mm, "end": v(-22.42, -56.62) * mm});
            skArc(sketch, "E13.22.7", {"start": v(-21.73, -57.16) * mm, "mid": v(-21.84, -56.92) * mm, "end": v(-22.05, -56.77) * mm});
            skArc(sketch, "E13.22.8", {"start": v(-21.51, -59.6) * mm, "mid": v(-21.57, -58.37) * mm, "end": v(-21.73, -57.16) * mm});
            skPoint(sketch, "E13.22.9", {"position": v(-21.5, -59.75) * mm});
            skArc(sketch, "E13.22.10", {"start": v(-21.56, -59.88) * mm, "mid": v(-21.52, -59.74) * mm, "end": v(-21.51, -59.6) * mm});
            skLineSegment(sketch, "E13.22.11", {"start": v(-21.56, -59.88) * mm, "end": v(-22.09, -61.35) * mm});
            skArc(sketch, "E13.22.12", {"start": v(-22.09, -61.35) * mm, "mid": v(-22.06, -61.99) * mm, "end": v(-21.58, -62.41) * mm});
            skArc(sketch, "E13.23.0", {"start": v(-19.23, -63.18) * mm, "mid": v(-18.6, -63.12) * mm, "end": v(-18.2, -62.62) * mm});
            skLineSegment(sketch, "E13.23.1", {"start": v(-17.76, -61.12) * mm, "end": v(-18.2, -62.62) * mm});
            skArc(sketch, "E13.23.2", {"start": v(-17.63, -60.86) * mm, "mid": v(-17.7, -60.98) * mm, "end": v(-17.76, -61.12) * mm});
            skArc(sketch, "E13.23.3", {"start": v(-17.63, -60.86) * mm, "mid": v(-16.86, -59.9) * mm, "end": v(-16.02, -59.02) * mm});
            skArc(sketch, "E13.23.4", {"start": v(-15.53, -58.89) * mm, "mid": v(-15.8, -58.89) * mm, "end": v(-16.02, -59.02) * mm});
            skLineSegment(sketch, "E13.23.5", {"start": v(-15.53, -58.89) * mm, "end": v(-15.15, -58.99) * mm});
            skLineSegment(sketch, "E13.23.6", {"start": v(-14.76, -59.09) * mm, "end": v(-15.15, -58.99) * mm});
            skArc(sketch, "E13.23.7", {"start": v(-14.4, -59.43) * mm, "mid": v(-14.53, -59.21) * mm, "end": v(-14.76, -59.09) * mm});
            skArc(sketch, "E13.23.8", {"start": v(-13.87, -61.82) * mm, "mid": v(-14.09, -60.62) * mm, "end": v(-14.4, -59.43) * mm});
            skPoint(sketch, "E13.23.9", {"position": v(-13.85, -61.97) * mm});
            skArc(sketch, "E13.23.10", {"start": v(-13.88, -62.11) * mm, "mid": v(-13.87, -61.97) * mm, "end": v(-13.87, -61.82) * mm});
            skLineSegment(sketch, "E13.23.11", {"start": v(-13.88, -62.11) * mm, "end": v(-14.22, -63.64) * mm});
            skArc(sketch, "E13.23.12", {"start": v(-14.22, -63.64) * mm, "mid": v(-14.11, -64.27) * mm, "end": v(-13.59, -64.63) * mm});
            skArc(sketch, "E13.24.0", {"start": v(-11.16, -65.1) * mm, "mid": v(-10.54, -64.95) * mm, "end": v(-10.2, -64.4) * mm});
            skLineSegment(sketch, "E13.24.1", {"start": v(-9.96, -62.86) * mm, "end": v(-10.2, -64.4) * mm});
            skArc(sketch, "E13.24.2", {"start": v(-9.86, -62.59) * mm, "mid": v(-9.92, -62.72) * mm, "end": v(-9.96, -62.86) * mm});
            skArc(sketch, "E13.24.3", {"start": v(-9.86, -62.59) * mm, "mid": v(-9.21, -61.55) * mm, "end": v(-8.5, -60.56) * mm});
            skArc(sketch, "E13.24.4", {"start": v(-8.03, -60.37) * mm, "mid": v(-8.29, -60.4) * mm, "end": v(-8.5, -60.56) * mm});
            skLineSegment(sketch, "E13.24.5", {"start": v(-8.03, -60.37) * mm, "end": v(-7.63, -60.42) * mm});
            skLineSegment(sketch, "E13.24.6", {"start": v(-7.24, -60.47) * mm, "end": v(-7.63, -60.42) * mm});
            skArc(sketch, "E13.24.7", {"start": v(-6.83, -60.77) * mm, "mid": v(-7, -60.57) * mm, "end": v(-7.24, -60.47) * mm});
            skArc(sketch, "E13.24.8", {"start": v(-6.01, -63.07) * mm, "mid": v(-6.38, -61.9) * mm, "end": v(-6.83, -60.77) * mm});
            skPoint(sketch, "E13.24.9", {"position": v(-5.98, -63.22) * mm});
            skArc(sketch, "E13.24.10", {"start": v(-5.99, -63.37) * mm, "mid": v(-5.99, -63.22) * mm, "end": v(-6.01, -63.07) * mm});
            skLineSegment(sketch, "E13.24.11", {"start": v(-5.99, -63.37) * mm, "end": v(-6.14, -64.92) * mm});
            skArc(sketch, "E13.24.12", {"start": v(-6.14, -64.92) * mm, "mid": v(-5.95, -65.53) * mm, "end": v(-5.38, -65.82) * mm});
            skArc(sketch, "E13.25.0", {"start": v(-2.9, -65.98) * mm, "mid": v(-2.31, -65.76) * mm, "end": v(-2.05, -65.18) * mm});
            skLineSegment(sketch, "E13.25.1", {"start": v(-2, -63.62) * mm, "end": v(-2.05, -65.18) * mm});
            skArc(sketch, "E13.25.2", {"start": v(-1.94, -63.33) * mm, "mid": v(-1.98, -63.47) * mm, "end": v(-2, -63.62) * mm});
            skArc(sketch, "E13.25.3", {"start": v(-1.94, -63.33) * mm, "mid": v(-1.43, -62.22) * mm, "end": v(-0.84, -61.15) * mm});
            skArc(sketch, "E13.25.4", {"start": v(-0.4, -60.9) * mm, "mid": v(-0.65, -60.97) * mm, "end": v(-0.84, -61.15) * mm});
            skLineSegment(sketch, "E13.25.5", {"start": v(-0.4, -60.9) * mm, "end": v(0, -60.9) * mm});
            skLineSegment(sketch, "E13.25.6", {"start": v(0.4, -60.9) * mm, "end": v(0, -60.9) * mm});
            skArc(sketch, "E13.25.7", {"start": v(0.84, -61.15) * mm, "mid": v(0.65, -60.97) * mm, "end": v(0.4, -60.9) * mm});
            skArc(sketch, "E13.25.8", {"start": v(1.94, -63.33) * mm, "mid": v(1.43, -62.22) * mm, "end": v(0.84, -61.15) * mm});
            skPoint(sketch, "E13.25.9", {"position": v(2, -63.47) * mm});
            skArc(sketch, "E13.25.10", {"start": v(2, -63.62) * mm, "mid": v(1.98, -63.47) * mm, "end": v(1.94, -63.33) * mm});
            skLineSegment(sketch, "E13.25.11", {"start": v(2, -63.62) * mm, "end": v(2.05, -65.18) * mm});
            skArc(sketch, "E13.25.12", {"start": v(2.05, -65.18) * mm, "mid": v(2.31, -65.76) * mm, "end": v(2.9, -65.98) * mm});
            skArc(sketch, "E13.26.0", {"start": v(5.38, -65.82) * mm, "mid": v(5.95, -65.53) * mm, "end": v(6.14, -64.92) * mm});
            skLineSegment(sketch, "E13.26.1", {"start": v(5.99, -63.37) * mm, "end": v(6.14, -64.92) * mm});
            skArc(sketch, "E13.26.2", {"start": v(6.01, -63.07) * mm, "mid": v(5.99, -63.22) * mm, "end": v(5.99, -63.37) * mm});
            skArc(sketch, "E13.26.3", {"start": v(6.01, -63.07) * mm, "mid": v(6.38, -61.9) * mm, "end": v(6.83, -60.77) * mm});
            skArc(sketch, "E13.26.4", {"start": v(7.24, -60.47) * mm, "mid": v(7, -60.57) * mm, "end": v(6.83, -60.77) * mm});
            skLineSegment(sketch, "E13.26.5", {"start": v(7.24, -60.47) * mm, "end": v(7.63, -60.42) * mm});
            skLineSegment(sketch, "E13.26.6", {"start": v(8.03, -60.37) * mm, "end": v(7.63, -60.42) * mm});
            skArc(sketch, "E13.26.7", {"start": v(8.5, -60.56) * mm, "mid": v(8.29, -60.4) * mm, "end": v(8.03, -60.37) * mm});
            skArc(sketch, "E13.26.8", {"start": v(9.86, -62.59) * mm, "mid": v(9.21, -61.55) * mm, "end": v(8.5, -60.56) * mm});
            skPoint(sketch, "E13.26.9", {"position": v(9.93, -62.72) * mm});
            skArc(sketch, "E13.26.10", {"start": v(9.96, -62.86) * mm, "mid": v(9.92, -62.72) * mm, "end": v(9.86, -62.59) * mm});
            skLineSegment(sketch, "E13.26.11", {"start": v(9.96, -62.86) * mm, "end": v(10.2, -64.4) * mm});
            skArc(sketch, "E13.26.12", {"start": v(10.2, -64.4) * mm, "mid": v(10.54, -64.95) * mm, "end": v(11.16, -65.1) * mm});
            skArc(sketch, "E13.27.0", {"start": v(13.59, -64.63) * mm, "mid": v(14.11, -64.27) * mm, "end": v(14.22, -63.64) * mm});
            skLineSegment(sketch, "E13.27.1", {"start": v(13.88, -62.11) * mm, "end": v(14.22, -63.64) * mm});
            skArc(sketch, "E13.27.2", {"start": v(13.87, -61.82) * mm, "mid": v(13.87, -61.97) * mm, "end": v(13.88, -62.11) * mm});
            skArc(sketch, "E13.27.3", {"start": v(13.87, -61.82) * mm, "mid": v(14.09, -60.62) * mm, "end": v(14.4, -59.43) * mm});
            skArc(sketch, "E13.27.4", {"start": v(14.76, -59.09) * mm, "mid": v(14.53, -59.21) * mm, "end": v(14.4, -59.43) * mm});
            skLineSegment(sketch, "E13.27.5", {"start": v(14.76, -59.09) * mm, "end": v(15.15, -58.99) * mm});
            skLineSegment(sketch, "E13.27.6", {"start": v(15.53, -58.89) * mm, "end": v(15.15, -58.99) * mm});
            skArc(sketch, "E13.27.7", {"start": v(16.02, -59.02) * mm, "mid": v(15.8, -58.89) * mm, "end": v(15.53, -58.89) * mm});
            skArc(sketch, "E13.27.8", {"start": v(17.63, -60.86) * mm, "mid": v(16.86, -59.9) * mm, "end": v(16.02, -59.02) * mm});
            skPoint(sketch, "E13.27.9", {"position": v(17.72, -60.98) * mm});
            skArc(sketch, "E13.27.10", {"start": v(17.76, -61.12) * mm, "mid": v(17.7, -60.98) * mm, "end": v(17.63, -60.86) * mm});
            skLineSegment(sketch, "E13.27.11", {"start": v(17.76, -61.12) * mm, "end": v(18.2, -62.62) * mm});
            skArc(sketch, "E13.27.12", {"start": v(18.2, -62.62) * mm, "mid": v(18.6, -63.12) * mm, "end": v(19.23, -63.18) * mm});
            skArc(sketch, "E13.28.0", {"start": v(21.58, -62.41) * mm, "mid": v(22.06, -61.99) * mm, "end": v(22.09, -61.35) * mm});
            skLineSegment(sketch, "E13.28.1", {"start": v(21.56, -59.88) * mm, "end": v(22.09, -61.35) * mm});
            skArc(sketch, "E13.28.2", {"start": v(21.51, -59.6) * mm, "mid": v(21.52, -59.74) * mm, "end": v(21.56, -59.88) * mm});
            skArc(sketch, "E13.28.3", {"start": v(21.51, -59.6) * mm, "mid": v(21.57, -58.37) * mm, "end": v(21.73, -57.16) * mm});
            skArc(sketch, "E13.28.4", {"start": v(22.05, -56.77) * mm, "mid": v(21.84, -56.92) * mm, "end": v(21.73, -57.16) * mm});
            skLineSegment(sketch, "E13.28.5", {"start": v(22.05, -56.77) * mm, "end": v(22.42, -56.62) * mm});
            skLineSegment(sketch, "E13.28.6", {"start": v(22.8, -56.48) * mm, "end": v(22.42, -56.62) * mm});
            skArc(sketch, "E13.28.7", {"start": v(23.29, -56.54) * mm, "mid": v(23.05, -56.45) * mm, "end": v(22.8, -56.48) * mm});
            skArc(sketch, "E13.28.8", {"start": v(25.11, -58.17) * mm, "mid": v(24.23, -57.32) * mm, "end": v(23.29, -56.54) * mm});
            skPoint(sketch, "E13.28.9", {"position": v(25.22, -58.28) * mm});
            skArc(sketch, "E13.28.10", {"start": v(25.28, -58.41) * mm, "mid": v(25.2, -58.28) * mm, "end": v(25.11, -58.17) * mm});
            skLineSegment(sketch, "E13.28.11", {"start": v(25.28, -58.41) * mm, "end": v(25.9, -59.85) * mm});
            skArc(sketch, "E13.28.12", {"start": v(25.9, -59.85) * mm, "mid": v(26.36, -60.29) * mm, "end": v(27, -60.27) * mm});
            skArc(sketch, "E13.29.0", {"start": v(29.23, -59.22) * mm, "mid": v(29.65, -58.74) * mm, "end": v(29.6, -58.1) * mm});
            skLineSegment(sketch, "E13.29.1", {"start": v(28.9, -56.71) * mm, "end": v(29.6, -58.1) * mm});
            skArc(sketch, "E13.29.2", {"start": v(28.81, -56.43) * mm, "mid": v(28.84, -56.57) * mm, "end": v(28.9, -56.71) * mm});
            skArc(sketch, "E13.29.3", {"start": v(28.81, -56.43) * mm, "mid": v(28.72, -55.2) * mm, "end": v(28.73, -53.98) * mm});
            skArc(sketch, "E13.29.4", {"start": v(28.99, -53.56) * mm, "mid": v(28.8, -53.74) * mm, "end": v(28.73, -53.98) * mm});
            skLineSegment(sketch, "E13.29.5", {"start": v(28.99, -53.56) * mm, "end": v(29.34, -53.37) * mm});
            skLineSegment(sketch, "E13.29.6", {"start": v(29.7, -53.17) * mm, "end": v(29.34, -53.37) * mm});
            skArc(sketch, "E13.29.7", {"start": v(30.19, -53.18) * mm, "mid": v(29.94, -53.11) * mm, "end": v(29.7, -53.17) * mm});
            skArc(sketch, "E13.29.8", {"start": v(32.2, -54.56) * mm, "mid": v(31.22, -53.83) * mm, "end": v(30.19, -53.18) * mm});
            skPoint(sketch, "E13.29.9", {"position": v(32.32, -54.66) * mm});
            skArc(sketch, "E13.29.10", {"start": v(32.4, -54.78) * mm, "mid": v(32.31, -54.66) * mm, "end": v(32.2, -54.56) * mm});
            skLineSegment(sketch, "E13.29.11", {"start": v(32.4, -54.78) * mm, "end": v(33.2, -56.13) * mm});
            skArc(sketch, "E13.29.12", {"start": v(33.2, -56.13) * mm, "mid": v(33.7, -56.5) * mm, "end": v(34.33, -56.41) * mm});
            skArc(sketch, "E13.30.0", {"start": v(36.43, -55.09) * mm, "mid": v(36.78, -54.56) * mm, "end": v(36.65, -53.93) * mm});
            skLineSegment(sketch, "E13.30.1", {"start": v(35.78, -52.64) * mm, "end": v(36.65, -53.93) * mm});
            skArc(sketch, "E13.30.2", {"start": v(35.66, -52.37) * mm, "mid": v(35.7, -52.51) * mm, "end": v(35.78, -52.64) * mm});
            skArc(sketch, "E13.30.3", {"start": v(35.66, -52.37) * mm, "mid": v(35.41, -51.17) * mm, "end": v(35.26, -49.96) * mm});
            skArc(sketch, "E13.30.4", {"start": v(35.47, -49.5) * mm, "mid": v(35.3, -49.7) * mm, "end": v(35.26, -49.96) * mm});
            skLineSegment(sketch, "E13.30.5", {"start": v(35.47, -49.5) * mm, "end": v(35.8, -49.27) * mm});
            skLineSegment(sketch, "E13.30.6", {"start": v(36.12, -49.03) * mm, "end": v(35.8, -49.27) * mm});
            skArc(sketch, "E13.30.7", {"start": v(36.62, -48.98) * mm, "mid": v(36.36, -48.94) * mm, "end": v(36.12, -49.03) * mm});
            skArc(sketch, "E13.30.8", {"start": v(38.8, -50.1) * mm, "mid": v(37.73, -49.5) * mm, "end": v(36.62, -48.98) * mm});
            skPoint(sketch, "E13.30.9", {"position": v(38.92, -50.17) * mm});
            skArc(sketch, "E13.30.10", {"start": v(39.01, -50.3) * mm, "mid": v(38.9, -50.18) * mm, "end": v(38.8, -50.1) * mm});
            skLineSegment(sketch, "E13.30.11", {"start": v(39.01, -50.3) * mm, "end": v(39.97, -51.53) * mm});
            skArc(sketch, "E13.30.12", {"start": v(39.97, -51.53) * mm, "mid": v(40.52, -51.84) * mm, "end": v(41.13, -51.67) * mm});
            skArc(sketch, "E13.31.0", {"start": v(43.04, -50.09) * mm, "mid": v(43.33, -49.52) * mm, "end": v(43.12, -48.91) * mm});
            skLineSegment(sketch, "E13.31.1", {"start": v(42.1, -47.74) * mm, "end": v(43.12, -48.91) * mm});
            skArc(sketch, "E13.31.2", {"start": v(41.94, -47.5) * mm, "mid": v(42, -47.62) * mm, "end": v(42.1, -47.74) * mm});
            skArc(sketch, "E13.31.3", {"start": v(41.94, -47.5) * mm, "mid": v(41.55, -46.33) * mm, "end": v(41.25, -45.15) * mm});
            skArc(sketch, "E13.31.4", {"start": v(41.4, -44.67) * mm, "mid": v(41.26, -44.89) * mm, "end": v(41.25, -45.15) * mm});
            skLineSegment(sketch, "E13.31.5", {"start": v(41.4, -44.67) * mm, "end": v(41.69, -44.4) * mm});
            skLineSegment(sketch, "E13.31.6", {"start": v(41.98, -44.12) * mm, "end": v(41.69, -44.4) * mm});
            skArc(sketch, "E13.31.7", {"start": v(42.47, -44) * mm, "mid": v(42.2, -44) * mm, "end": v(41.98, -44.12) * mm});
            skArc(sketch, "E13.31.8", {"start": v(44.76, -44.84) * mm, "mid": v(43.63, -44.38) * mm, "end": v(42.47, -44) * mm});
            skPoint(sketch, "E13.31.9", {"position": v(44.9, -44.9) * mm});
            skArc(sketch, "E13.31.10", {"start": v(45, -45) * mm, "mid": v(44.9, -44.91) * mm, "end": v(44.76, -44.84) * mm});
            skLineSegment(sketch, "E13.31.11", {"start": v(45, -45) * mm, "end": v(46.1, -46.1) * mm});
            skArc(sketch, "E13.31.12", {"start": v(46.1, -46.1) * mm, "mid": v(46.7, -46.35) * mm, "end": v(47.28, -46.1) * mm});
            skArc(sketch, "E13.32.0", {"start": v(48.98, -44.3) * mm, "mid": v(49.2, -43.7) * mm, "end": v(48.91, -43.12) * mm});
            skLineSegment(sketch, "E13.32.1", {"start": v(47.74, -42.1) * mm, "end": v(48.91, -43.12) * mm});
            skArc(sketch, "E13.32.2", {"start": v(47.56, -41.86) * mm, "mid": v(47.64, -41.98) * mm, "end": v(47.74, -42.1) * mm});
            skArc(sketch, "E13.32.3", {"start": v(47.56, -41.86) * mm, "mid": v(47.03, -40.76) * mm, "end": v(46.58, -39.62) * mm});
            skArc(sketch, "E13.32.4", {"start": v(46.67, -39.13) * mm, "mid": v(46.56, -39.36) * mm, "end": v(46.58, -39.62) * mm});
            skLineSegment(sketch, "E13.32.5", {"start": v(46.67, -39.13) * mm, "end": v(46.92, -38.82) * mm});
            skLineSegment(sketch, "E13.32.6", {"start": v(47.18, -38.51) * mm, "end": v(46.92, -38.82) * mm});
            skArc(sketch, "E13.32.7", {"start": v(47.65, -38.33) * mm, "mid": v(47.39, -38.36) * mm, "end": v(47.18, -38.51) * mm});
            skArc(sketch, "E13.32.8", {"start": v(50.03, -38.87) * mm, "mid": v(48.85, -38.56) * mm, "end": v(47.65, -38.33) * mm});
            skPoint(sketch, "E13.32.9", {"position": v(50.17, -38.92) * mm});
            skArc(sketch, "E13.32.10", {"start": v(50.3, -39.01) * mm, "mid": v(50.17, -38.93) * mm, "end": v(50.03, -38.87) * mm});
            skLineSegment(sketch, "E13.32.11", {"start": v(50.3, -39.01) * mm, "end": v(51.53, -39.97) * mm});
            skArc(sketch, "E13.32.12", {"start": v(51.53, -39.97) * mm, "mid": v(52.14, -40.13) * mm, "end": v(52.7, -39.81) * mm});
            skArc(sketch, "E13.33.0", {"start": v(54.15, -37.8) * mm, "mid": v(54.28, -37.19) * mm, "end": v(53.93, -36.65) * mm});
            skLineSegment(sketch, "E13.33.1", {"start": v(52.64, -35.78) * mm, "end": v(53.93, -36.65) * mm});
            skArc(sketch, "E13.33.2", {"start": v(52.43, -35.57) * mm, "mid": v(52.53, -35.68) * mm, "end": v(52.64, -35.78) * mm});
            skArc(sketch, "E13.33.3", {"start": v(52.43, -35.57) * mm, "mid": v(51.76, -34.54) * mm, "end": v(51.18, -33.47) * mm});
            skArc(sketch, "E13.33.4", {"start": v(51.2, -32.97) * mm, "mid": v(51.13, -33.22) * mm, "end": v(51.18, -33.47) * mm});
            skLineSegment(sketch, "E13.33.5", {"start": v(51.2, -32.97) * mm, "end": v(51.42, -32.63) * mm});
            skLineSegment(sketch, "E13.33.6", {"start": v(51.64, -32.3) * mm, "end": v(51.42, -32.63) * mm});
            skArc(sketch, "E13.33.7", {"start": v(52.07, -32.06) * mm, "mid": v(51.82, -32.12) * mm, "end": v(51.64, -32.3) * mm});
            skArc(sketch, "E13.33.8", {"start": v(54.5, -32.3) * mm, "mid": v(53.3, -32.13) * mm, "end": v(52.07, -32.06) * mm});
            skPoint(sketch, "E13.33.9", {"position": v(54.66, -32.32) * mm});
            skArc(sketch, "E13.33.10", {"start": v(54.78, -32.4) * mm, "mid": v(54.65, -32.34) * mm, "end": v(54.5, -32.3) * mm});
            skLineSegment(sketch, "E13.33.11", {"start": v(54.78, -32.4) * mm, "end": v(56.13, -33.2) * mm});
            skArc(sketch, "E13.33.12", {"start": v(56.13, -33.2) * mm, "mid": v(56.76, -33.28) * mm, "end": v(57.26, -32.9) * mm});
            skArc(sketch, "E13.34.0", {"start": v(58.46, -30.72) * mm, "mid": v(58.51, -30.09) * mm, "end": v(58.1, -29.6) * mm});
            skLineSegment(sketch, "E13.34.1", {"start": v(56.71, -28.9) * mm, "end": v(58.1, -29.6) * mm});
            skArc(sketch, "E13.34.2", {"start": v(56.48, -28.72) * mm, "mid": v(56.59, -28.82) * mm, "end": v(56.71, -28.9) * mm});
            skArc(sketch, "E13.34.3", {"start": v(56.48, -28.72) * mm, "mid": v(55.69, -27.78) * mm, "end": v(54.97, -26.8) * mm});
            skArc(sketch, "E13.34.4", {"start": v(54.93, -26.3) * mm, "mid": v(54.89, -26.55) * mm, "end": v(54.97, -26.8) * mm});
            skLineSegment(sketch, "E13.34.5", {"start": v(54.93, -26.3) * mm, "end": v(55.1, -25.93) * mm});
            skLineSegment(sketch, "E13.34.6", {"start": v(55.28, -25.57) * mm, "end": v(55.1, -25.93) * mm});
            skArc(sketch, "E13.34.7", {"start": v(55.68, -25.28) * mm, "mid": v(55.44, -25.37) * mm, "end": v(55.28, -25.57) * mm});
            skArc(sketch, "E13.34.8", {"start": v(58.13, -25.21) * mm, "mid": v(56.9, -25.2) * mm, "end": v(55.68, -25.28) * mm});
            skPoint(sketch, "E13.34.9", {"position": v(58.28, -25.22) * mm});
            skArc(sketch, "E13.34.10", {"start": v(58.41, -25.28) * mm, "mid": v(58.27, -25.23) * mm, "end": v(58.13, -25.21) * mm});
            skLineSegment(sketch, "E13.34.11", {"start": v(58.41, -25.28) * mm, "end": v(59.85, -25.9) * mm});
            skArc(sketch, "E13.34.12", {"start": v(59.85, -25.9) * mm, "mid": v(60.48, -25.9) * mm, "end": v(60.94, -25.46) * mm});
            skArc(sketch, "E13.35.0", {"start": v(61.85, -23.15) * mm, "mid": v(61.82, -22.52) * mm, "end": v(61.35, -22.09) * mm});
            skLineSegment(sketch, "E13.35.1", {"start": v(59.88, -21.56) * mm, "end": v(61.35, -22.09) * mm});
            skArc(sketch, "E13.35.2", {"start": v(59.63, -21.41) * mm, "mid": v(59.75, -21.5) * mm, "end": v(59.88, -21.56) * mm});
            skArc(sketch, "E13.35.3", {"start": v(59.63, -21.41) * mm, "mid": v(58.73, -20.58) * mm, "end": v(57.9, -19.69) * mm});
            skArc(sketch, "E13.35.4", {"start": v(57.8, -19.2) * mm, "mid": v(57.78, -19.46) * mm, "end": v(57.9, -19.69) * mm});
            skLineSegment(sketch, "E13.35.5", {"start": v(57.8, -19.2) * mm, "end": v(57.92, -18.82) * mm});
            skLineSegment(sketch, "E13.35.6", {"start": v(58.04, -18.44) * mm, "end": v(57.92, -18.82) * mm});
            skArc(sketch, "E13.35.7", {"start": v(58.41, -18.1) * mm, "mid": v(58.18, -18.22) * mm, "end": v(58.04, -18.44) * mm});
            skArc(sketch, "E13.35.8", {"start": v(60.83, -17.73) * mm, "mid": v(59.61, -17.87) * mm, "end": v(58.41, -18.1) * mm});
            skPoint(sketch, "E13.35.9", {"position": v(60.98, -17.72) * mm});
            skArc(sketch, "E13.35.10", {"start": v(61.12, -17.76) * mm, "mid": v(60.98, -17.73) * mm, "end": v(60.83, -17.73) * mm});
            skLineSegment(sketch, "E13.35.11", {"start": v(61.12, -17.76) * mm, "end": v(62.62, -18.2) * mm});
            skArc(sketch, "E13.35.12", {"start": v(62.62, -18.2) * mm, "mid": v(63.25, -18.12) * mm, "end": v(63.65, -17.62) * mm});
            skArc(sketch, "E13.36.0", {"start": v(64.26, -15.22) * mm, "mid": v(64.16, -14.6) * mm, "end": v(63.64, -14.22) * mm});
            skLineSegment(sketch, "E13.36.1", {"start": v(62.11, -13.88) * mm, "end": v(63.64, -14.22) * mm});
            skArc(sketch, "E13.36.2", {"start": v(61.84, -13.77) * mm, "mid": v(61.97, -13.84) * mm, "end": v(62.11, -13.88) * mm});
            skArc(sketch, "E13.36.3", {"start": v(61.84, -13.77) * mm, "mid": v(60.85, -13.06) * mm, "end": v(59.9, -12.28) * mm});
            skArc(sketch, "E13.36.4", {"start": v(59.75, -11.8) * mm, "mid": v(59.76, -12.06) * mm, "end": v(59.9, -12.28) * mm});
            skLineSegment(sketch, "E13.36.5", {"start": v(59.75, -11.8) * mm, "end": v(59.82, -11.41) * mm});
            skLineSegment(sketch, "E13.36.6", {"start": v(59.9, -11.02) * mm, "end": v(59.82, -11.41) * mm});
            skArc(sketch, "E13.36.7", {"start": v(60.22, -10.64) * mm, "mid": v(60, -10.79) * mm, "end": v(59.9, -11.02) * mm});
            skArc(sketch, "E13.36.8", {"start": v(62.57, -9.96) * mm, "mid": v(61.38, -10.25) * mm, "end": v(60.22, -10.64) * mm});
            skPoint(sketch, "E13.36.9", {"position": v(62.72, -9.93) * mm});
            skArc(sketch, "E13.36.10", {"start": v(62.86, -9.96) * mm, "mid": v(62.72, -9.95) * mm, "end": v(62.57, -9.96) * mm});
            skLineSegment(sketch, "E13.36.11", {"start": v(62.86, -9.96) * mm, "end": v(64.4, -10.2) * mm});
            skArc(sketch, "E13.36.12", {"start": v(64.4, -10.2) * mm, "mid": v(65.03, -10.05) * mm, "end": v(65.35, -9.5) * mm});
            skArc(sketch, "E13.37.0", {"start": v(65.66, -7.05) * mm, "mid": v(65.48, -6.44) * mm, "end": v(64.92, -6.14) * mm});
            skLineSegment(sketch, "E13.37.1", {"start": v(63.37, -5.99) * mm, "end": v(64.92, -6.14) * mm});
            skArc(sketch, "E13.37.2", {"start": v(63.08, -5.91) * mm, "mid": v(63.22, -5.96) * mm, "end": v(63.37, -5.99) * mm});
            skArc(sketch, "E13.37.3", {"start": v(63.08, -5.91) * mm, "mid": v(62, -5.33) * mm, "end": v(60.97, -4.67) * mm});
            skArc(sketch, "E13.37.4", {"start": v(60.76, -4.22) * mm, "mid": v(60.8, -4.48) * mm, "end": v(60.97, -4.67) * mm});
            skLineSegment(sketch, "E13.37.5", {"start": v(60.76, -4.22) * mm, "end": v(60.78, -3.82) * mm});
            skLineSegment(sketch, "E13.37.6", {"start": v(60.8, -3.42) * mm, "end": v(60.78, -3.82) * mm});
            skArc(sketch, "E13.37.7", {"start": v(61.08, -3) * mm, "mid": v(60.89, -3.18) * mm, "end": v(60.8, -3.42) * mm});
            skArc(sketch, "E13.37.8", {"start": v(63.32, -2.04) * mm, "mid": v(62.18, -2.48) * mm, "end": v(61.08, -3) * mm});
            skPoint(sketch, "E13.37.9", {"position": v(63.47, -2) * mm});
            skArc(sketch, "E13.37.10", {"start": v(63.62, -2) * mm, "mid": v(63.47, -2) * mm, "end": v(63.32, -2.04) * mm});
            skLineSegment(sketch, "E13.37.11", {"start": v(63.62, -2) * mm, "end": v(65.18, -2.05) * mm});
            skArc(sketch, "E13.37.12", {"start": v(65.18, -2.05) * mm, "mid": v(65.77, -1.82) * mm, "end": v(66.03, -1.24) * mm});
            skArc(sketch, "E13.38.0", {"start": v(66.03, 1.24) * mm, "mid": v(65.77, 1.82) * mm, "end": v(65.18, 2.05) * mm});
            skLineSegment(sketch, "E13.38.1", {"start": v(63.62, 2) * mm, "end": v(65.18, 2.05) * mm});
            skArc(sketch, "E13.38.2", {"start": v(63.32, 2.04) * mm, "mid": v(63.47, 2) * mm, "end": v(63.62, 2) * mm});
            skArc(sketch, "E13.38.3", {"start": v(63.32, 2.04) * mm, "mid": v(62.18, 2.48) * mm, "end": v(61.08, 3) * mm});
            skArc(sketch, "E13.38.4", {"start": v(60.8, 3.42) * mm, "mid": v(60.89, 3.18) * mm, "end": v(61.08, 3) * mm});
            skLineSegment(sketch, "E13.38.5", {"start": v(60.8, 3.42) * mm, "end": v(60.78, 3.82) * mm});
            skLineSegment(sketch, "E13.38.6", {"start": v(60.76, 4.22) * mm, "end": v(60.78, 3.82) * mm});
            skArc(sketch, "E13.38.7", {"start": v(60.97, 4.67) * mm, "mid": v(60.8, 4.48) * mm, "end": v(60.76, 4.22) * mm});
            skArc(sketch, "E13.38.8", {"start": v(63.08, 5.91) * mm, "mid": v(62, 5.33) * mm, "end": v(60.97, 4.67) * mm});
            skPoint(sketch, "E13.38.9", {"position": v(63.22, 5.98) * mm});
            skArc(sketch, "E13.38.10", {"start": v(63.37, 5.99) * mm, "mid": v(63.22, 5.96) * mm, "end": v(63.08, 5.91) * mm});
            skLineSegment(sketch, "E13.38.11", {"start": v(63.37, 5.99) * mm, "end": v(64.92, 6.14) * mm});
            skArc(sketch, "E13.38.12", {"start": v(64.92, 6.14) * mm, "mid": v(65.48, 6.44) * mm, "end": v(65.66, 7.05) * mm});
            skArc(sketch, "E13.39.0", {"start": v(65.35, 9.5) * mm, "mid": v(65.03, 10.05) * mm, "end": v(64.4, 10.2) * mm});
            skLineSegment(sketch, "E13.39.1", {"start": v(62.86, 9.96) * mm, "end": v(64.4, 10.2) * mm});
            skArc(sketch, "E13.39.2", {"start": v(62.57, 9.96) * mm, "mid": v(62.72, 9.95) * mm, "end": v(62.86, 9.96) * mm});
            skArc(sketch, "E13.39.3", {"start": v(62.57, 9.96) * mm, "mid": v(61.38, 10.25) * mm, "end": v(60.22, 10.64) * mm});
            skArc(sketch, "E13.39.4", {"start": v(59.9, 11.02) * mm, "mid": v(60, 10.79) * mm, "end": v(60.22, 10.64) * mm});
            skLineSegment(sketch, "E13.39.5", {"start": v(59.9, 11.02) * mm, "end": v(59.82, 11.41) * mm});
            skLineSegment(sketch, "E13.39.6", {"start": v(59.75, 11.8) * mm, "end": v(59.82, 11.41) * mm});
            skArc(sketch, "E13.39.7", {"start": v(59.9, 12.28) * mm, "mid": v(59.76, 12.06) * mm, "end": v(59.75, 11.8) * mm});
            skArc(sketch, "E13.39.8", {"start": v(61.84, 13.77) * mm, "mid": v(60.85, 13.06) * mm, "end": v(59.9, 12.28) * mm});
            skPoint(sketch, "E13.39.9", {"position": v(61.97, 13.85) * mm});
            skArc(sketch, "E13.39.10", {"start": v(62.11, 13.88) * mm, "mid": v(61.97, 13.84) * mm, "end": v(61.84, 13.77) * mm});
            skLineSegment(sketch, "E13.39.11", {"start": v(62.11, 13.88) * mm, "end": v(63.64, 14.22) * mm});
            skArc(sketch, "E13.39.12", {"start": v(63.64, 14.22) * mm, "mid": v(64.16, 14.6) * mm, "end": v(64.26, 15.22) * mm});
            skArc(sketch, "E13.40.0", {"start": v(63.65, 17.62) * mm, "mid": v(63.25, 18.12) * mm, "end": v(62.62, 18.2) * mm});
            skLineSegment(sketch, "E13.40.1", {"start": v(61.12, 17.76) * mm, "end": v(62.62, 18.2) * mm});
            skArc(sketch, "E13.40.2", {"start": v(60.83, 17.73) * mm, "mid": v(60.98, 17.73) * mm, "end": v(61.12, 17.76) * mm});
            skArc(sketch, "E13.40.3", {"start": v(60.83, 17.73) * mm, "mid": v(59.61, 17.87) * mm, "end": v(58.41, 18.1) * mm});
            skArc(sketch, "E13.40.4", {"start": v(58.04, 18.44) * mm, "mid": v(58.18, 18.22) * mm, "end": v(58.41, 18.1) * mm});
            skLineSegment(sketch, "E13.40.5", {"start": v(58.04, 18.44) * mm, "end": v(57.92, 18.82) * mm});
            skLineSegment(sketch, "E13.40.6", {"start": v(57.8, 19.2) * mm, "end": v(57.92, 18.82) * mm});
            skArc(sketch, "E13.40.7", {"start": v(57.9, 19.69) * mm, "mid": v(57.78, 19.46) * mm, "end": v(57.8, 19.2) * mm});
            skArc(sketch, "E13.40.8", {"start": v(59.63, 21.41) * mm, "mid": v(58.73, 20.58) * mm, "end": v(57.9, 19.69) * mm});
            skPoint(sketch, "E13.40.9", {"position": v(59.75, 21.5) * mm});
            skArc(sketch, "E13.40.10", {"start": v(59.88, 21.56) * mm, "mid": v(59.75, 21.5) * mm, "end": v(59.63, 21.41) * mm});
            skLineSegment(sketch, "E13.40.11", {"start": v(59.88, 21.56) * mm, "end": v(61.35, 22.09) * mm});
            skArc(sketch, "E13.40.12", {"start": v(61.35, 22.09) * mm, "mid": v(61.82, 22.52) * mm, "end": v(61.85, 23.15) * mm});
            skArc(sketch, "E13.41.0", {"start": v(60.94, 25.46) * mm, "mid": v(60.48, 25.9) * mm, "end": v(59.85, 25.9) * mm});
            skLineSegment(sketch, "E13.41.1", {"start": v(58.41, 25.28) * mm, "end": v(59.85, 25.9) * mm});
            skArc(sketch, "E13.41.2", {"start": v(58.13, 25.21) * mm, "mid": v(58.27, 25.23) * mm, "end": v(58.41, 25.28) * mm});
            skArc(sketch, "E13.41.3", {"start": v(58.13, 25.21) * mm, "mid": v(56.9, 25.2) * mm, "end": v(55.68, 25.28) * mm});
            skArc(sketch, "E13.41.4", {"start": v(55.28, 25.57) * mm, "mid": v(55.44, 25.37) * mm, "end": v(55.68, 25.28) * mm});
            skLineSegment(sketch, "E13.41.5", {"start": v(55.28, 25.57) * mm, "end": v(55.1, 25.93) * mm});
            skLineSegment(sketch, "E13.41.6", {"start": v(54.93, 26.3) * mm, "end": v(55.1, 25.93) * mm});
            skArc(sketch, "E13.41.7", {"start": v(54.97, 26.8) * mm, "mid": v(54.89, 26.55) * mm, "end": v(54.93, 26.3) * mm});
            skArc(sketch, "E13.41.8", {"start": v(56.48, 28.72) * mm, "mid": v(55.69, 27.78) * mm, "end": v(54.97, 26.8) * mm});
            skPoint(sketch, "E13.41.9", {"position": v(56.58, 28.83) * mm});
            skArc(sketch, "E13.41.10", {"start": v(56.71, 28.9) * mm, "mid": v(56.59, 28.82) * mm, "end": v(56.48, 28.72) * mm});
            skLineSegment(sketch, "E13.41.11", {"start": v(56.71, 28.9) * mm, "end": v(58.1, 29.6) * mm});
            skArc(sketch, "E13.41.12", {"start": v(58.1, 29.6) * mm, "mid": v(58.51, 30.09) * mm, "end": v(58.46, 30.72) * mm});
            skArc(sketch, "E13.42.0", {"start": v(57.26, 32.9) * mm, "mid": v(56.76, 33.28) * mm, "end": v(56.13, 33.2) * mm});
            skLineSegment(sketch, "E13.42.1", {"start": v(54.78, 32.4) * mm, "end": v(56.13, 33.2) * mm});
            skArc(sketch, "E13.42.2", {"start": v(54.5, 32.3) * mm, "mid": v(54.65, 32.34) * mm, "end": v(54.78, 32.4) * mm});
            skArc(sketch, "E13.42.3", {"start": v(54.5, 32.3) * mm, "mid": v(53.3, 32.13) * mm, "end": v(52.07, 32.06) * mm});
            skArc(sketch, "E13.42.4", {"start": v(51.64, 32.3) * mm, "mid": v(51.82, 32.12) * mm, "end": v(52.07, 32.06) * mm});
            skLineSegment(sketch, "E13.42.5", {"start": v(51.64, 32.3) * mm, "end": v(51.42, 32.63) * mm});
            skLineSegment(sketch, "E13.42.6", {"start": v(51.2, 32.97) * mm, "end": v(51.42, 32.63) * mm});
            skArc(sketch, "E13.42.7", {"start": v(51.18, 33.47) * mm, "mid": v(51.13, 33.22) * mm, "end": v(51.2, 32.97) * mm});
            skArc(sketch, "E13.42.8", {"start": v(52.43, 35.57) * mm, "mid": v(51.76, 34.54) * mm, "end": v(51.18, 33.47) * mm});
            skPoint(sketch, "E13.42.9", {"position": v(52.52, 35.7) * mm});
            skArc(sketch, "E13.42.10", {"start": v(52.64, 35.78) * mm, "mid": v(52.53, 35.68) * mm, "end": v(52.43, 35.57) * mm});
            skLineSegment(sketch, "E13.42.11", {"start": v(52.64, 35.78) * mm, "end": v(53.93, 36.65) * mm});
            skArc(sketch, "E13.42.12", {"start": v(53.93, 36.65) * mm, "mid": v(54.28, 37.19) * mm, "end": v(54.15, 37.8) * mm});
            skArc(sketch, "E13.43.0", {"start": v(52.7, 39.81) * mm, "mid": v(52.14, 40.13) * mm, "end": v(51.53, 39.97) * mm});
            skLineSegment(sketch, "E13.43.1", {"start": v(50.3, 39.01) * mm, "end": v(51.53, 39.97) * mm});
            skArc(sketch, "E13.43.2", {"start": v(50.03, 38.87) * mm, "mid": v(50.17, 38.93) * mm, "end": v(50.3, 39.01) * mm});
            skArc(sketch, "E13.43.3", {"start": v(50.03, 38.87) * mm, "mid": v(48.85, 38.56) * mm, "end": v(47.65, 38.33) * mm});
            skArc(sketch, "E13.43.4", {"start": v(47.18, 38.51) * mm, "mid": v(47.39, 38.36) * mm, "end": v(47.65, 38.33) * mm});
            skLineSegment(sketch, "E13.43.5", {"start": v(47.18, 38.51) * mm, "end": v(46.92, 38.82) * mm});
            skLineSegment(sketch, "E13.43.6", {"start": v(46.67, 39.13) * mm, "end": v(46.92, 38.82) * mm});
            skArc(sketch, "E13.43.7", {"start": v(46.58, 39.62) * mm, "mid": v(46.56, 39.36) * mm, "end": v(46.67, 39.13) * mm});
            skArc(sketch, "E13.43.8", {"start": v(47.56, 41.86) * mm, "mid": v(47.03, 40.76) * mm, "end": v(46.58, 39.62) * mm});
            skPoint(sketch, "E13.43.9", {"position": v(47.63, 42) * mm});
            skArc(sketch, "E13.43.10", {"start": v(47.74, 42.1) * mm, "mid": v(47.64, 41.98) * mm, "end": v(47.56, 41.86) * mm});
            skLineSegment(sketch, "E13.43.11", {"start": v(47.74, 42.1) * mm, "end": v(48.91, 43.12) * mm});
            skArc(sketch, "E13.43.12", {"start": v(48.91, 43.12) * mm, "mid": v(49.2, 43.7) * mm, "end": v(48.98, 44.3) * mm});
            skArc(sketch, "E13.44.0", {"start": v(47.28, 46.1) * mm, "mid": v(46.7, 46.35) * mm, "end": v(46.1, 46.1) * mm});
            skLineSegment(sketch, "E13.44.1", {"start": v(45, 45) * mm, "end": v(46.1, 46.1) * mm});
            skArc(sketch, "E13.44.2", {"start": v(44.76, 44.84) * mm, "mid": v(44.9, 44.91) * mm, "end": v(45, 45) * mm});
            skArc(sketch, "E13.44.3", {"start": v(44.76, 44.84) * mm, "mid": v(43.63, 44.38) * mm, "end": v(42.47, 44) * mm});
            skArc(sketch, "E13.44.4", {"start": v(41.98, 44.12) * mm, "mid": v(42.2, 44) * mm, "end": v(42.47, 44) * mm});
            skLineSegment(sketch, "E13.44.5", {"start": v(41.98, 44.12) * mm, "end": v(41.69, 44.4) * mm});
            skLineSegment(sketch, "E13.44.6", {"start": v(41.4, 44.67) * mm, "end": v(41.69, 44.4) * mm});
            skArc(sketch, "E13.44.7", {"start": v(41.25, 45.15) * mm, "mid": v(41.26, 44.89) * mm, "end": v(41.4, 44.67) * mm});
            skArc(sketch, "E13.44.8", {"start": v(41.94, 47.5) * mm, "mid": v(41.55, 46.33) * mm, "end": v(41.25, 45.15) * mm});
            skPoint(sketch, "E13.44.9", {"position": v(42, 47.63) * mm});
            skArc(sketch, "E13.44.10", {"start": v(42.1, 47.74) * mm, "mid": v(42, 47.62) * mm, "end": v(41.94, 47.5) * mm});
            skLineSegment(sketch, "E13.44.11", {"start": v(42.1, 47.74) * mm, "end": v(43.12, 48.91) * mm});
            skArc(sketch, "E13.44.12", {"start": v(43.12, 48.91) * mm, "mid": v(43.33, 49.52) * mm, "end": v(43.04, 50.09) * mm});
            skArc(sketch, "E13.45.0", {"start": v(41.13, 51.67) * mm, "mid": v(40.52, 51.84) * mm, "end": v(39.97, 51.53) * mm});
            skLineSegment(sketch, "E13.45.1", {"start": v(39.01, 50.3) * mm, "end": v(39.97, 51.53) * mm});
            skArc(sketch, "E13.45.2", {"start": v(38.8, 50.1) * mm, "mid": v(38.9, 50.18) * mm, "end": v(39.01, 50.3) * mm});
            skArc(sketch, "E13.45.3", {"start": v(38.8, 50.1) * mm, "mid": v(37.73, 49.5) * mm, "end": v(36.62, 48.98) * mm});
            skArc(sketch, "E13.45.4", {"start": v(36.12, 49.03) * mm, "mid": v(36.36, 48.94) * mm, "end": v(36.62, 48.98) * mm});
            skLineSegment(sketch, "E13.45.5", {"start": v(36.12, 49.03) * mm, "end": v(35.8, 49.27) * mm});
            skLineSegment(sketch, "E13.45.6", {"start": v(35.47, 49.5) * mm, "end": v(35.8, 49.27) * mm});
            skArc(sketch, "E13.45.7", {"start": v(35.26, 49.96) * mm, "mid": v(35.3, 49.7) * mm, "end": v(35.47, 49.5) * mm});
            skArc(sketch, "E13.45.8", {"start": v(35.66, 52.37) * mm, "mid": v(35.41, 51.17) * mm, "end": v(35.26, 49.96) * mm});
            skPoint(sketch, "E13.45.9", {"position": v(35.7, 52.52) * mm});
            skArc(sketch, "E13.45.10", {"start": v(35.78, 52.64) * mm, "mid": v(35.7, 52.51) * mm, "end": v(35.66, 52.37) * mm});
            skLineSegment(sketch, "E13.45.11", {"start": v(35.78, 52.64) * mm, "end": v(36.65, 53.93) * mm});
            skArc(sketch, "E13.45.12", {"start": v(36.65, 53.93) * mm, "mid": v(36.78, 54.56) * mm, "end": v(36.43, 55.09) * mm});
            skArc(sketch, "E13.46.0", {"start": v(34.33, 56.41) * mm, "mid": v(33.7, 56.5) * mm, "end": v(33.2, 56.13) * mm});
            skLineSegment(sketch, "E13.46.1", {"start": v(32.4, 54.78) * mm, "end": v(33.2, 56.13) * mm});
            skArc(sketch, "E13.46.2", {"start": v(32.2, 54.56) * mm, "mid": v(32.31, 54.66) * mm, "end": v(32.4, 54.78) * mm});
            skArc(sketch, "E13.46.3", {"start": v(32.2, 54.56) * mm, "mid": v(31.22, 53.83) * mm, "end": v(30.19, 53.18) * mm});
            skArc(sketch, "E13.46.4", {"start": v(29.7, 53.17) * mm, "mid": v(29.94, 53.11) * mm, "end": v(30.19, 53.18) * mm});
            skLineSegment(sketch, "E13.46.5", {"start": v(29.7, 53.17) * mm, "end": v(29.34, 53.37) * mm});
            skLineSegment(sketch, "E13.46.6", {"start": v(28.99, 53.56) * mm, "end": v(29.34, 53.37) * mm});
            skArc(sketch, "E13.46.7", {"start": v(28.73, 53.98) * mm, "mid": v(28.8, 53.74) * mm, "end": v(28.99, 53.56) * mm});
            skArc(sketch, "E13.46.8", {"start": v(28.81, 56.43) * mm, "mid": v(28.72, 55.2) * mm, "end": v(28.73, 53.98) * mm});
            skPoint(sketch, "E13.46.9", {"position": v(28.83, 56.58) * mm});
            skArc(sketch, "E13.46.10", {"start": v(28.9, 56.71) * mm, "mid": v(28.84, 56.57) * mm, "end": v(28.81, 56.43) * mm});
            skLineSegment(sketch, "E13.46.11", {"start": v(28.9, 56.71) * mm, "end": v(29.6, 58.1) * mm});
            skArc(sketch, "E13.46.12", {"start": v(29.6, 58.1) * mm, "mid": v(29.65, 58.74) * mm, "end": v(29.23, 59.22) * mm});
            skArc(sketch, "E13.47.0", {"start": v(27, 60.27) * mm, "mid": v(26.36, 60.29) * mm, "end": v(25.9, 59.85) * mm});
            skLineSegment(sketch, "E13.47.1", {"start": v(25.28, 58.41) * mm, "end": v(25.9, 59.85) * mm});
            skArc(sketch, "E13.47.2", {"start": v(25.11, 58.17) * mm, "mid": v(25.2, 58.28) * mm, "end": v(25.28, 58.41) * mm});
            skArc(sketch, "E13.47.3", {"start": v(25.11, 58.17) * mm, "mid": v(24.23, 57.32) * mm, "end": v(23.29, 56.54) * mm});
            skArc(sketch, "E13.47.4", {"start": v(22.8, 56.48) * mm, "mid": v(23.05, 56.45) * mm, "end": v(23.29, 56.54) * mm});
            skLineSegment(sketch, "E13.47.5", {"start": v(22.8, 56.48) * mm, "end": v(22.42, 56.62) * mm});
            skLineSegment(sketch, "E13.47.6", {"start": v(22.05, 56.77) * mm, "end": v(22.42, 56.62) * mm});
            skArc(sketch, "E13.47.7", {"start": v(21.73, 57.16) * mm, "mid": v(21.84, 56.92) * mm, "end": v(22.05, 56.77) * mm});
            skArc(sketch, "E13.47.8", {"start": v(21.51, 59.6) * mm, "mid": v(21.57, 58.37) * mm, "end": v(21.73, 57.16) * mm});
            skPoint(sketch, "E13.47.9", {"position": v(21.5, 59.75) * mm});
            skArc(sketch, "E13.47.10", {"start": v(21.56, 59.88) * mm, "mid": v(21.52, 59.74) * mm, "end": v(21.51, 59.6) * mm});
            skLineSegment(sketch, "E13.47.11", {"start": v(21.56, 59.88) * mm, "end": v(22.09, 61.35) * mm});
            skArc(sketch, "E13.47.12", {"start": v(22.09, 61.35) * mm, "mid": v(22.06, 61.99) * mm, "end": v(21.58, 62.41) * mm});
            skArc(sketch, "E13.48.0", {"start": v(19.23, 63.18) * mm, "mid": v(18.6, 63.12) * mm, "end": v(18.2, 62.62) * mm});
            skLineSegment(sketch, "E13.48.1", {"start": v(17.76, 61.12) * mm, "end": v(18.2, 62.62) * mm});
            skArc(sketch, "E13.48.2", {"start": v(17.63, 60.86) * mm, "mid": v(17.7, 60.98) * mm, "end": v(17.76, 61.12) * mm});
            skArc(sketch, "E13.48.3", {"start": v(17.63, 60.86) * mm, "mid": v(16.86, 59.9) * mm, "end": v(16.02, 59.02) * mm});
            skArc(sketch, "E13.48.4", {"start": v(15.53, 58.89) * mm, "mid": v(15.8, 58.89) * mm, "end": v(16.02, 59.02) * mm});
            skLineSegment(sketch, "E13.48.5", {"start": v(15.53, 58.89) * mm, "end": v(15.15, 58.99) * mm});
            skLineSegment(sketch, "E13.48.6", {"start": v(14.76, 59.09) * mm, "end": v(15.15, 58.99) * mm});
            skArc(sketch, "E13.48.7", {"start": v(14.4, 59.43) * mm, "mid": v(14.53, 59.21) * mm, "end": v(14.76, 59.09) * mm});
            skArc(sketch, "E13.48.8", {"start": v(13.87, 61.82) * mm, "mid": v(14.09, 60.62) * mm, "end": v(14.4, 59.43) * mm});
            skPoint(sketch, "E13.48.9", {"position": v(13.85, 61.97) * mm});
            skArc(sketch, "E13.48.10", {"start": v(13.88, 62.11) * mm, "mid": v(13.87, 61.97) * mm, "end": v(13.87, 61.82) * mm});
            skLineSegment(sketch, "E13.48.11", {"start": v(13.88, 62.11) * mm, "end": v(14.22, 63.64) * mm});
            skArc(sketch, "E13.48.12", {"start": v(14.22, 63.64) * mm, "mid": v(14.11, 64.27) * mm, "end": v(13.59, 64.63) * mm});
            skArc(sketch, "E13.49.0", {"start": v(11.16, 65.1) * mm, "mid": v(10.54, 64.95) * mm, "end": v(10.2, 64.4) * mm});
            skLineSegment(sketch, "E13.49.1", {"start": v(9.96, 62.86) * mm, "end": v(10.2, 64.4) * mm});
            skArc(sketch, "E13.49.2", {"start": v(9.86, 62.59) * mm, "mid": v(9.92, 62.72) * mm, "end": v(9.96, 62.86) * mm});
            skArc(sketch, "E13.49.3", {"start": v(9.86, 62.59) * mm, "mid": v(9.21, 61.55) * mm, "end": v(8.5, 60.56) * mm});
            skArc(sketch, "E13.49.4", {"start": v(8.03, 60.37) * mm, "mid": v(8.29, 60.4) * mm, "end": v(8.5, 60.56) * mm});
            skLineSegment(sketch, "E13.49.5", {"start": v(8.03, 60.37) * mm, "end": v(7.63, 60.42) * mm});
            skLineSegment(sketch, "E13.49.6", {"start": v(7.24, 60.47) * mm, "end": v(7.63, 60.42) * mm});
            skArc(sketch, "E13.49.7", {"start": v(6.83, 60.77) * mm, "mid": v(7, 60.57) * mm, "end": v(7.24, 60.47) * mm});
            skArc(sketch, "E13.49.8", {"start": v(6.01, 63.07) * mm, "mid": v(6.38, 61.9) * mm, "end": v(6.83, 60.77) * mm});
            skPoint(sketch, "E13.49.9", {"position": v(5.98, 63.22) * mm});
            skArc(sketch, "E13.49.10", {"start": v(5.99, 63.37) * mm, "mid": v(5.99, 63.22) * mm, "end": v(6.01, 63.07) * mm});
            skLineSegment(sketch, "E13.49.11", {"start": v(5.99, 63.37) * mm, "end": v(6.14, 64.92) * mm});
            skArc(sketch, "E13.49.12", {"start": v(6.14, 64.92) * mm, "mid": v(5.95, 65.53) * mm, "end": v(5.38, 65.82) * mm});
            skArc(sketch, "E14.trimOffspring", {"start": v(5.38, 65.82) * mm, "mid": v(4.15, 65.9) * mm, "end": v(2.9, 65.98) * mm});
            skArc(sketch, "E15.trimOffspring", {"start": v(13.59, 64.63) * mm, "mid": v(12.37, 64.87) * mm, "end": v(11.16, 65.1) * mm});
            skArc(sketch, "E16.trimOffspring", {"start": v(21.58, 62.41) * mm, "mid": v(20.4, 62.8) * mm, "end": v(19.23, 63.18) * mm});
            skArc(sketch, "E17.trimOffspring", {"start": v(29.23, 59.22) * mm, "mid": v(28.12, 59.75) * mm, "end": v(27, 60.27) * mm});
            skArc(sketch, "E18.trimOffspring", {"start": v(36.43, 55.09) * mm, "mid": v(35.39, 55.76) * mm, "end": v(34.33, 56.41) * mm});
            skArc(sketch, "E19.trimOffspring", {"start": v(43.04, 50.09) * mm, "mid": v(42.1, 50.88) * mm, "end": v(41.13, 51.67) * mm});
            skArc(sketch, "E20.trimOffspring", {"start": v(48.98, 44.3) * mm, "mid": v(48.14, 45.2) * mm, "end": v(47.28, 46.1) * mm});
            skArc(sketch, "E21.trimOffspring", {"start": v(-11.16, 65.1) * mm, "mid": v(-12.37, 64.87) * mm, "end": v(-13.59, 64.63) * mm});
            skArc(sketch, "E22.trimOffspring", {"start": v(-19.23, 63.18) * mm, "mid": v(-20.4, 62.8) * mm, "end": v(-21.58, 62.41) * mm});
            skArc(sketch, "E23.trimOffspring", {"start": v(-27, 60.27) * mm, "mid": v(-28.12, 59.75) * mm, "end": v(-29.23, 59.22) * mm});
            skArc(sketch, "E24.trimOffspring", {"start": v(-34.33, 56.41) * mm, "mid": v(-35.39, 55.76) * mm, "end": v(-36.43, 55.09) * mm});
            skArc(sketch, "E25.trimOffspring", {"start": v(-41.13, 51.67) * mm, "mid": v(-42.1, 50.88) * mm, "end": v(-43.04, 50.09) * mm});
            skArc(sketch, "E26.trimOffspring", {"start": v(-47.28, 46.1) * mm, "mid": v(-48.14, 45.2) * mm, "end": v(-48.98, 44.3) * mm});
            skArc(sketch, "E27.trimOffspring", {"start": v(-52.7, 39.81) * mm, "mid": v(-53.43, 38.82) * mm, "end": v(-54.15, 37.8) * mm});
            skArc(sketch, "E28.trimOffspring", {"start": v(-57.26, 32.9) * mm, "mid": v(-57.87, 31.82) * mm, "end": v(-58.46, 30.72) * mm});
            skArc(sketch, "E29.trimOffspring", {"start": v(-60.94, 25.46) * mm, "mid": v(-61.4, 24.31) * mm, "end": v(-61.85, 23.15) * mm});
            skArc(sketch, "E30.trimOffspring", {"start": v(-63.65, 17.62) * mm, "mid": v(-63.97, 16.42) * mm, "end": v(-64.26, 15.22) * mm});
            skArc(sketch, "E31.trimOffspring", {"start": v(-65.35, 9.5) * mm, "mid": v(-65.52, 8.28) * mm, "end": v(-65.66, 7.05) * mm});
            skArc(sketch, "E32.trimOffspring", {"start": v(54.15, 37.8) * mm, "mid": v(53.43, 38.82) * mm, "end": v(52.7, 39.81) * mm});
            skArc(sketch, "E33.trimOffspring", {"start": v(58.46, 30.72) * mm, "mid": v(57.87, 31.82) * mm, "end": v(57.26, 32.9) * mm});
            skArc(sketch, "E34.trimOffspring", {"start": v(61.85, 23.15) * mm, "mid": v(61.4, 24.31) * mm, "end": v(60.94, 25.46) * mm});
            skArc(sketch, "E35.trimOffspring", {"start": v(-66.03, 1.24) * mm, "mid": v(-66.04, 0) * mm, "end": v(-66.03, -1.24) * mm});
            skArc(sketch, "E36.trimOffspring", {"start": v(64.26, 15.22) * mm, "mid": v(63.97, 16.42) * mm, "end": v(63.65, 17.62) * mm});
            skArc(sketch, "E37.trimOffspring", {"start": v(65.66, 7.05) * mm, "mid": v(65.52, 8.28) * mm, "end": v(65.35, 9.5) * mm});
            skArc(sketch, "E38.trimOffspring", {"start": v(66.03, -1.24) * mm, "mid": v(66.04, 0) * mm, "end": v(66.03, 1.24) * mm});
            skArc(sketch, "E39.trimOffspring", {"start": v(-65.66, -7.05) * mm, "mid": v(-65.52, -8.28) * mm, "end": v(-65.35, -9.5) * mm});
            skArc(sketch, "E40.trimOffspring", {"start": v(65.35, -9.5) * mm, "mid": v(65.52, -8.28) * mm, "end": v(65.66, -7.05) * mm});
            skArc(sketch, "E41.trimOffspring", {"start": v(-61.85, -23.15) * mm, "mid": v(-61.4, -24.31) * mm, "end": v(-60.94, -25.46) * mm});
            skArc(sketch, "E42.trimOffspring", {"start": v(63.65, -17.62) * mm, "mid": v(63.97, -16.42) * mm, "end": v(64.26, -15.22) * mm});
            skArc(sketch, "E43.trimOffspring", {"start": v(60.94, -25.46) * mm, "mid": v(61.4, -24.31) * mm, "end": v(61.85, -23.15) * mm});
            skArc(sketch, "E44.trimOffspring", {"start": v(-58.46, -30.72) * mm, "mid": v(-57.87, -31.82) * mm, "end": v(-57.26, -32.9) * mm});
            skArc(sketch, "E45.trimOffspring", {"start": v(57.26, -32.9) * mm, "mid": v(57.87, -31.82) * mm, "end": v(58.46, -30.72) * mm});
            skArc(sketch, "E46.trimOffspring", {"start": v(-54.15, -37.8) * mm, "mid": v(-53.43, -38.82) * mm, "end": v(-52.7, -39.81) * mm});
            skArc(sketch, "E47.trimOffspring", {"start": v(-48.98, -44.3) * mm, "mid": v(-48.14, -45.2) * mm, "end": v(-47.28, -46.1) * mm});
            skArc(sketch, "E48.trimOffspring", {"start": v(-43.04, -50.09) * mm, "mid": v(-42.1, -50.88) * mm, "end": v(-41.13, -51.67) * mm});
            skArc(sketch, "E49.trimOffspring", {"start": v(-36.43, -55.09) * mm, "mid": v(-35.39, -55.76) * mm, "end": v(-34.33, -56.41) * mm});
            skArc(sketch, "E50.trimOffspring", {"start": v(-29.23, -59.22) * mm, "mid": v(-28.12, -59.75) * mm, "end": v(-27, -60.27) * mm});
            skArc(sketch, "E51.trimOffspring", {"start": v(-21.58, -62.41) * mm, "mid": v(-20.4, -62.8) * mm, "end": v(-19.23, -63.18) * mm});
            skArc(sketch, "E52.trimOffspring", {"start": v(-13.59, -64.63) * mm, "mid": v(-12.37, -64.87) * mm, "end": v(-11.16, -65.1) * mm});
            skArc(sketch, "E53.trimOffspring", {"start": v(-5.38, -65.82) * mm, "mid": v(-4.15, -65.9) * mm, "end": v(-2.9, -65.98) * mm});
            skArc(sketch, "E54.trimOffspring", {"start": v(2.9, -65.98) * mm, "mid": v(4.15, -65.9) * mm, "end": v(5.38, -65.82) * mm});
            skArc(sketch, "E55.trimOffspring", {"start": v(11.16, -65.1) * mm, "mid": v(12.37, -64.87) * mm, "end": v(13.59, -64.63) * mm});
            skArc(sketch, "E56.trimOffspring", {"start": v(19.23, -63.18) * mm, "mid": v(20.4, -62.8) * mm, "end": v(21.58, -62.41) * mm});
            skArc(sketch, "E57.trimOffspring", {"start": v(27, -60.27) * mm, "mid": v(28.12, -59.75) * mm, "end": v(29.23, -59.22) * mm});
            skArc(sketch, "E58.trimOffspring", {"start": v(34.33, -56.41) * mm, "mid": v(35.39, -55.76) * mm, "end": v(36.43, -55.09) * mm});
            skArc(sketch, "E59.trimOffspring", {"start": v(41.13, -51.67) * mm, "mid": v(42.1, -50.88) * mm, "end": v(43.04, -50.09) * mm});
            skArc(sketch, "E60.trimOffspring", {"start": v(47.28, -46.1) * mm, "mid": v(48.14, -45.2) * mm, "end": v(48.98, -44.3) * mm});
            skArc(sketch, "E61.trimOffspring", {"start": v(52.7, -39.81) * mm, "mid": v(53.43, -38.82) * mm, "end": v(54.15, -37.8) * mm});
            skCircle(sketch, "E62", {"center": v(0, 0) * mm, "radius": 71.12 * mm});
            skLineSegment(sketch, "E63", {"start": v(-64.26, -15.22) * mm, "end": v(-63.65, -17.62) * mm});
            skSolve(sketch);
        }
        {
            var Q0;
            Q0 = qSketchRegion(id + "F0", true);
            var Q1;
            Q1=makeQuery(id+"F0.imprint","IMPRINT",FACE,{"disambiguationData":[TD([[makeQuery(id+"F0.imprint","IMPRINT",EDGE,{"derivedFrom":sQuery(id+"F0.wireOp",EDGE,"E0")}),-1.0]])]});
            extrude(context, id + "F1", {"entities" : qUnion([Q0, Q1]), "depth" : 127 * mm});
        }
        {
            var Q0;
            Q0=makeQuery(id+"F1.opExtrude","CAP_FACE",FACE,{"disambiguationData":[OSD([sQuery(id+"F0.wireOp",EDGE,"E0"),sQuery(id+"F0.wireOp",EDGE,"E1.MirrorCS"),sQuery(id+"F0.wireOp",EDGE,"E2"),sQuery(id+"F0.wireOp",EDGE,"E3"),sQuery(id+"F0.wireOp",EDGE,"E4.MirrorCS"),sQuery(id+"F0.wireOp",EDGE,"E5.MirrorCS"),sQuery(id+"F0.wireOp",EDGE,"E6.MirrorCS"),sQuery(id+"F0.wireOp",EDGE,"E7.filletArc"),sQuery(id+"F0.wireOp",EDGE,"E8.filletArc"),sQuery(id+"F0.wireOp",EDGE,"E9.filletArc"),sQuery(id+"F0.wireOp",EDGE,"E10.filletArc"),sQuery(id+"F0.wireOp",EDGE,"E11.filletArc"),sQuery(id+"F0.wireOp",EDGE,"E12.filletArc"),sQuery(id+"F0.wireOp",EDGE,"E13.1.0"),sQuery(id+"F0.wireOp",EDGE,"E13.1.1"),sQuery(id+"F0.wireOp",EDGE,"E13.1.2"),sQuery(id+"F0.wireOp",EDGE,"E13.1.3"),sQuery(id+"F0.wireOp",EDGE,"E13.1.4"),sQuery(id+"F0.wireOp",EDGE,"E13.1.5"),sQuery(id+"F0.wireOp",EDGE,"E13.1.6"),sQuery(id+"F0.wireOp",EDGE,"E13.1.7"),sQuery(id+"F0.wireOp",EDGE,"E13.1.8"),sQuery(id+"F0.wireOp",EDGE,"E13.1.10"),sQuery(id+"F0.wireOp",EDGE,"E13.1.11"),sQuery(id+"F0.wireOp",EDGE,"E13.1.12"),sQuery(id+"F0.wireOp",EDGE,"E13.2.0"),sQuery(id+"F0.wireOp",EDGE,"E13.2.1"),sQuery(id+"F0.wireOp",EDGE,"E13.2.2"),sQuery(id+"F0.wireOp",EDGE,"E13.2.3"),sQuery(id+"F0.wireOp",EDGE,"E13.2.4"),sQuery(id+"F0.wireOp",EDGE,"E13.2.5"),sQuery(id+"F0.wireOp",EDGE,"E13.2.6"),sQuery(id+"F0.wireOp",EDGE,"E13.2.7"),sQuery(id+"F0.wireOp",EDGE,"E13.2.8"),sQuery(id+"F0.wireOp",EDGE,"E13.2.10"),sQuery(id+"F0.wireOp",EDGE,"E13.2.11"),sQuery(id+"F0.wireOp",EDGE,"E13.2.12"),sQuery(id+"F0.wireOp",EDGE,"E13.3.0"),sQuery(id+"F0.wireOp",EDGE,"E13.3.1"),sQuery(id+"F0.wireOp",EDGE,"E13.3.2"),sQuery(id+"F0.wireOp",EDGE,"E13.3.3"),sQuery(id+"F0.wireOp",EDGE,"E13.3.4"),sQuery(id+"F0.wireOp",EDGE,"E13.3.5"),sQuery(id+"F0.wireOp",EDGE,"E13.3.6"),sQuery(id+"F0.wireOp",EDGE,"E13.3.7"),sQuery(id+"F0.wireOp",EDGE,"E13.3.8"),sQuery(id+"F0.wireOp",EDGE,"E13.3.10"),sQuery(id+"F0.wireOp",EDGE,"E13.3.11"),sQuery(id+"F0.wireOp",EDGE,"E13.3.12"),sQuery(id+"F0.wireOp",EDGE,"E13.4.0"),sQuery(id+"F0.wireOp",EDGE,"E13.4.1"),sQuery(id+"F0.wireOp",EDGE,"E13.4.2"),sQuery(id+"F0.wireOp",EDGE,"E13.4.3"),sQuery(id+"F0.wireOp",EDGE,"E13.4.4"),sQuery(id+"F0.wireOp",EDGE,"E13.4.5"),sQuery(id+"F0.wireOp",EDGE,"E13.4.6"),sQuery(id+"F0.wireOp",EDGE,"E13.4.7"),sQuery(id+"F0.wireOp",EDGE,"E13.4.8"),sQuery(id+"F0.wireOp",EDGE,"E13.4.10"),sQuery(id+"F0.wireOp",EDGE,"E13.4.11"),sQuery(id+"F0.wireOp",EDGE,"E13.4.12"),sQuery(id+"F0.wireOp",EDGE,"E13.5.0"),sQuery(id+"F0.wireOp",EDGE,"E13.5.1"),sQuery(id+"F0.wireOp",EDGE,"E13.5.2"),sQuery(id+"F0.wireOp",EDGE,"E13.5.3"),sQuery(id+"F0.wireOp",EDGE,"E13.5.4"),sQuery(id+"F0.wireOp",EDGE,"E13.5.5"),sQuery(id+"F0.wireOp",EDGE,"E13.5.6"),sQuery(id+"F0.wireOp",EDGE,"E13.5.7"),sQuery(id+"F0.wireOp",EDGE,"E13.5.8"),sQuery(id+"F0.wireOp",EDGE,"E13.5.10"),sQuery(id+"F0.wireOp",EDGE,"E13.5.11"),sQuery(id+"F0.wireOp",EDGE,"E13.5.12"),sQuery(id+"F0.wireOp",EDGE,"E13.6.0"),sQuery(id+"F0.wireOp",EDGE,"E13.6.1"),sQuery(id+"F0.wireOp",EDGE,"E13.6.2"),sQuery(id+"F0.wireOp",EDGE,"E13.6.3"),sQuery(id+"F0.wireOp",EDGE,"E13.6.4"),sQuery(id+"F0.wireOp",EDGE,"E13.6.5"),sQuery(id+"F0.wireOp",EDGE,"E13.6.6"),sQuery(id+"F0.wireOp",EDGE,"E13.6.7"),sQuery(id+"F0.wireOp",EDGE,"E13.6.8"),sQuery(id+"F0.wireOp",EDGE,"E13.6.10"),sQuery(id+"F0.wireOp",EDGE,"E13.6.11"),sQuery(id+"F0.wireOp",EDGE,"E13.6.12"),sQuery(id+"F0.wireOp",EDGE,"E13.7.0"),sQuery(id+"F0.wireOp",EDGE,"E13.7.1"),sQuery(id+"F0.wireOp",EDGE,"E13.7.2"),sQuery(id+"F0.wireOp",EDGE,"E13.7.3"),sQuery(id+"F0.wireOp",EDGE,"E13.7.4"),sQuery(id+"F0.wireOp",EDGE,"E13.7.5"),sQuery(id+"F0.wireOp",EDGE,"E13.7.6"),sQuery(id+"F0.wireOp",EDGE,"E13.7.7"),sQuery(id+"F0.wireOp",EDGE,"E13.7.8"),sQuery(id+"F0.wireOp",EDGE,"E13.7.10"),sQuery(id+"F0.wireOp",EDGE,"E13.7.11"),sQuery(id+"F0.wireOp",EDGE,"E13.7.12"),sQuery(id+"F0.wireOp",EDGE,"E13.8.0"),sQuery(id+"F0.wireOp",EDGE,"E13.8.1"),sQuery(id+"F0.wireOp",EDGE,"E13.8.2"),sQuery(id+"F0.wireOp",EDGE,"E13.8.3"),sQuery(id+"F0.wireOp",EDGE,"E13.8.4"),sQuery(id+"F0.wireOp",EDGE,"E13.8.5"),sQuery(id+"F0.wireOp",EDGE,"E13.8.6"),sQuery(id+"F0.wireOp",EDGE,"E13.8.7"),sQuery(id+"F0.wireOp",EDGE,"E13.8.8"),sQuery(id+"F0.wireOp",EDGE,"E13.8.10"),sQuery(id+"F0.wireOp",EDGE,"E13.8.11"),sQuery(id+"F0.wireOp",EDGE,"E13.8.12"),sQuery(id+"F0.wireOp",EDGE,"E13.9.0"),sQuery(id+"F0.wireOp",EDGE,"E13.9.1"),sQuery(id+"F0.wireOp",EDGE,"E13.9.2"),sQuery(id+"F0.wireOp",EDGE,"E13.9.3"),sQuery(id+"F0.wireOp",EDGE,"E13.9.4"),sQuery(id+"F0.wireOp",EDGE,"E13.9.5"),sQuery(id+"F0.wireOp",EDGE,"E13.9.6"),sQuery(id+"F0.wireOp",EDGE,"E13.9.7"),sQuery(id+"F0.wireOp",EDGE,"E13.9.8"),sQuery(id+"F0.wireOp",EDGE,"E13.9.10"),sQuery(id+"F0.wireOp",EDGE,"E13.9.11"),sQuery(id+"F0.wireOp",EDGE,"E13.9.12"),sQuery(id+"F0.wireOp",EDGE,"E13.10.0"),sQuery(id+"F0.wireOp",EDGE,"E13.10.1"),sQuery(id+"F0.wireOp",EDGE,"E13.10.2"),sQuery(id+"F0.wireOp",EDGE,"E13.10.3"),sQuery(id+"F0.wireOp",EDGE,"E13.10.4"),sQuery(id+"F0.wireOp",EDGE,"E13.10.5"),sQuery(id+"F0.wireOp",EDGE,"E13.10.6"),sQuery(id+"F0.wireOp",EDGE,"E13.10.7"),sQuery(id+"F0.wireOp",EDGE,"E13.10.8"),sQuery(id+"F0.wireOp",EDGE,"E13.10.10"),sQuery(id+"F0.wireOp",EDGE,"E13.10.11"),sQuery(id+"F0.wireOp",EDGE,"E13.10.12"),sQuery(id+"F0.wireOp",EDGE,"E13.11.0"),sQuery(id+"F0.wireOp",EDGE,"E13.11.1"),sQuery(id+"F0.wireOp",EDGE,"E13.11.2"),sQuery(id+"F0.wireOp",EDGE,"E13.11.3"),sQuery(id+"F0.wireOp",EDGE,"E13.11.4"),sQuery(id+"F0.wireOp",EDGE,"E13.11.5"),sQuery(id+"F0.wireOp",EDGE,"E13.11.6"),sQuery(id+"F0.wireOp",EDGE,"E13.11.7"),sQuery(id+"F0.wireOp",EDGE,"E13.11.8"),sQuery(id+"F0.wireOp",EDGE,"E13.11.10"),sQuery(id+"F0.wireOp",EDGE,"E13.11.11"),sQuery(id+"F0.wireOp",EDGE,"E13.11.12"),sQuery(id+"F0.wireOp",EDGE,"E13.12.0"),sQuery(id+"F0.wireOp",EDGE,"E13.12.1"),sQuery(id+"F0.wireOp",EDGE,"E13.12.2"),sQuery(id+"F0.wireOp",EDGE,"E13.12.3"),sQuery(id+"F0.wireOp",EDGE,"E13.12.4"),sQuery(id+"F0.wireOp",EDGE,"E13.12.5"),sQuery(id+"F0.wireOp",EDGE,"E13.12.6"),sQuery(id+"F0.wireOp",EDGE,"E13.12.7"),sQuery(id+"F0.wireOp",EDGE,"E13.12.8"),sQuery(id+"F0.wireOp",EDGE,"E13.12.10"),sQuery(id+"F0.wireOp",EDGE,"E13.12.11"),sQuery(id+"F0.wireOp",EDGE,"E13.12.12"),sQuery(id+"F0.wireOp",EDGE,"E13.13.0"),sQuery(id+"F0.wireOp",EDGE,"E13.13.1"),sQuery(id+"F0.wireOp",EDGE,"E13.13.2"),sQuery(id+"F0.wireOp",EDGE,"E13.13.3"),sQuery(id+"F0.wireOp",EDGE,"E13.13.4"),sQuery(id+"F0.wireOp",EDGE,"E13.13.5"),sQuery(id+"F0.wireOp",EDGE,"E13.13.6"),sQuery(id+"F0.wireOp",EDGE,"E13.13.7"),sQuery(id+"F0.wireOp",EDGE,"E13.13.8"),sQuery(id+"F0.wireOp",EDGE,"E13.13.10"),sQuery(id+"F0.wireOp",EDGE,"E13.13.11"),sQuery(id+"F0.wireOp",EDGE,"E13.13.12"),sQuery(id+"F0.wireOp",EDGE,"E13.14.0"),sQuery(id+"F0.wireOp",EDGE,"E13.14.1"),sQuery(id+"F0.wireOp",EDGE,"E13.14.2"),sQuery(id+"F0.wireOp",EDGE,"E13.14.3"),sQuery(id+"F0.wireOp",EDGE,"E13.14.4"),sQuery(id+"F0.wireOp",EDGE,"E13.14.5"),sQuery(id+"F0.wireOp",EDGE,"E13.14.6"),sQuery(id+"F0.wireOp",EDGE,"E13.14.7"),sQuery(id+"F0.wireOp",EDGE,"E13.14.8"),sQuery(id+"F0.wireOp",EDGE,"E13.14.10"),sQuery(id+"F0.wireOp",EDGE,"E13.14.11"),sQuery(id+"F0.wireOp",EDGE,"E13.14.12"),sQuery(id+"F0.wireOp",EDGE,"E13.15.0"),sQuery(id+"F0.wireOp",EDGE,"E13.15.1"),sQuery(id+"F0.wireOp",EDGE,"E13.15.2"),sQuery(id+"F0.wireOp",EDGE,"E13.15.3"),sQuery(id+"F0.wireOp",EDGE,"E13.15.4"),sQuery(id+"F0.wireOp",EDGE,"E13.15.5"),sQuery(id+"F0.wireOp",EDGE,"E13.15.6"),sQuery(id+"F0.wireOp",EDGE,"E13.15.7"),sQuery(id+"F0.wireOp",EDGE,"E13.15.8"),sQuery(id+"F0.wireOp",EDGE,"E13.15.10"),sQuery(id+"F0.wireOp",EDGE,"E13.15.11"),sQuery(id+"F0.wireOp",EDGE,"E13.15.12"),sQuery(id+"F0.wireOp",EDGE,"E13.16.0"),sQuery(id+"F0.wireOp",EDGE,"E13.16.1"),sQuery(id+"F0.wireOp",EDGE,"E13.16.2"),sQuery(id+"F0.wireOp",EDGE,"E13.16.3"),sQuery(id+"F0.wireOp",EDGE,"E13.16.4"),sQuery(id+"F0.wireOp",EDGE,"E13.16.5"),sQuery(id+"F0.wireOp",EDGE,"E13.16.6"),sQuery(id+"F0.wireOp",EDGE,"E13.16.7"),sQuery(id+"F0.wireOp",EDGE,"E13.16.8"),sQuery(id+"F0.wireOp",EDGE,"E13.16.10"),sQuery(id+"F0.wireOp",EDGE,"E13.16.11"),sQuery(id+"F0.wireOp",EDGE,"E13.16.12"),sQuery(id+"F0.wireOp",EDGE,"E13.17.0"),sQuery(id+"F0.wireOp",EDGE,"E13.17.1"),sQuery(id+"F0.wireOp",EDGE,"E13.17.2"),sQuery(id+"F0.wireOp",EDGE,"E13.17.3"),sQuery(id+"F0.wireOp",EDGE,"E13.17.4"),sQuery(id+"F0.wireOp",EDGE,"E13.17.5"),sQuery(id+"F0.wireOp",EDGE,"E13.17.6"),sQuery(id+"F0.wireOp",EDGE,"E13.17.7"),sQuery(id+"F0.wireOp",EDGE,"E13.17.8"),sQuery(id+"F0.wireOp",EDGE,"E13.17.10"),sQuery(id+"F0.wireOp",EDGE,"E13.17.11"),sQuery(id+"F0.wireOp",EDGE,"E13.17.12"),sQuery(id+"F0.wireOp",EDGE,"E13.18.0"),sQuery(id+"F0.wireOp",EDGE,"E13.18.1"),sQuery(id+"F0.wireOp",EDGE,"E13.18.2"),sQuery(id+"F0.wireOp",EDGE,"E13.18.3"),sQuery(id+"F0.wireOp",EDGE,"E13.18.4"),sQuery(id+"F0.wireOp",EDGE,"E13.18.5"),sQuery(id+"F0.wireOp",EDGE,"E13.18.6"),sQuery(id+"F0.wireOp",EDGE,"E13.18.7"),sQuery(id+"F0.wireOp",EDGE,"E13.18.8"),sQuery(id+"F0.wireOp",EDGE,"E13.18.10"),sQuery(id+"F0.wireOp",EDGE,"E13.18.11"),sQuery(id+"F0.wireOp",EDGE,"E13.18.12"),sQuery(id+"F0.wireOp",EDGE,"E13.19.0"),sQuery(id+"F0.wireOp",EDGE,"E13.19.1"),sQuery(id+"F0.wireOp",EDGE,"E13.19.2"),sQuery(id+"F0.wireOp",EDGE,"E13.19.3"),sQuery(id+"F0.wireOp",EDGE,"E13.19.4"),sQuery(id+"F0.wireOp",EDGE,"E13.19.5"),sQuery(id+"F0.wireOp",EDGE,"E13.19.6"),sQuery(id+"F0.wireOp",EDGE,"E13.19.7"),sQuery(id+"F0.wireOp",EDGE,"E13.19.8"),sQuery(id+"F0.wireOp",EDGE,"E13.19.10"),sQuery(id+"F0.wireOp",EDGE,"E13.19.11"),sQuery(id+"F0.wireOp",EDGE,"E13.19.12"),sQuery(id+"F0.wireOp",EDGE,"E13.20.0"),sQuery(id+"F0.wireOp",EDGE,"E13.20.1"),sQuery(id+"F0.wireOp",EDGE,"E13.20.2"),sQuery(id+"F0.wireOp",EDGE,"E13.20.3"),sQuery(id+"F0.wireOp",EDGE,"E13.20.4"),sQuery(id+"F0.wireOp",EDGE,"E13.20.5"),sQuery(id+"F0.wireOp",EDGE,"E13.20.6"),sQuery(id+"F0.wireOp",EDGE,"E13.20.7"),sQuery(id+"F0.wireOp",EDGE,"E13.20.8"),sQuery(id+"F0.wireOp",EDGE,"E13.20.10"),sQuery(id+"F0.wireOp",EDGE,"E13.20.11"),sQuery(id+"F0.wireOp",EDGE,"E13.20.12"),sQuery(id+"F0.wireOp",EDGE,"E13.21.0"),sQuery(id+"F0.wireOp",EDGE,"E13.21.1"),sQuery(id+"F0.wireOp",EDGE,"E13.21.2"),sQuery(id+"F0.wireOp",EDGE,"E13.21.3"),sQuery(id+"F0.wireOp",EDGE,"E13.21.4"),sQuery(id+"F0.wireOp",EDGE,"E13.21.5"),sQuery(id+"F0.wireOp",EDGE,"E13.21.6"),sQuery(id+"F0.wireOp",EDGE,"E13.21.7"),sQuery(id+"F0.wireOp",EDGE,"E13.21.8"),sQuery(id+"F0.wireOp",EDGE,"E13.21.10"),sQuery(id+"F0.wireOp",EDGE,"E13.21.11"),sQuery(id+"F0.wireOp",EDGE,"E13.21.12"),sQuery(id+"F0.wireOp",EDGE,"E13.22.0"),sQuery(id+"F0.wireOp",EDGE,"E13.22.1"),sQuery(id+"F0.wireOp",EDGE,"E13.22.2"),sQuery(id+"F0.wireOp",EDGE,"E13.22.3"),sQuery(id+"F0.wireOp",EDGE,"E13.22.4"),sQuery(id+"F0.wireOp",EDGE,"E13.22.5"),sQuery(id+"F0.wireOp",EDGE,"E13.22.6"),sQuery(id+"F0.wireOp",EDGE,"E13.22.7"),sQuery(id+"F0.wireOp",EDGE,"E13.22.8"),sQuery(id+"F0.wireOp",EDGE,"E13.22.10"),sQuery(id+"F0.wireOp",EDGE,"E13.22.11"),sQuery(id+"F0.wireOp",EDGE,"E13.22.12"),sQuery(id+"F0.wireOp",EDGE,"E13.23.0"),sQuery(id+"F0.wireOp",EDGE,"E13.23.1"),sQuery(id+"F0.wireOp",EDGE,"E13.23.2"),sQuery(id+"F0.wireOp",EDGE,"E13.23.3"),sQuery(id+"F0.wireOp",EDGE,"E13.23.4"),sQuery(id+"F0.wireOp",EDGE,"E13.23.5"),sQuery(id+"F0.wireOp",EDGE,"E13.23.6"),sQuery(id+"F0.wireOp",EDGE,"E13.23.7"),sQuery(id+"F0.wireOp",EDGE,"E13.23.8"),sQuery(id+"F0.wireOp",EDGE,"E13.23.10"),sQuery(id+"F0.wireOp",EDGE,"E13.23.11"),sQuery(id+"F0.wireOp",EDGE,"E13.23.12"),sQuery(id+"F0.wireOp",EDGE,"E13.24.0"),sQuery(id+"F0.wireOp",EDGE,"E13.24.1"),sQuery(id+"F0.wireOp",EDGE,"E13.24.2"),sQuery(id+"F0.wireOp",EDGE,"E13.24.3"),sQuery(id+"F0.wireOp",EDGE,"E13.24.4"),sQuery(id+"F0.wireOp",EDGE,"E13.24.5"),sQuery(id+"F0.wireOp",EDGE,"E13.24.6"),sQuery(id+"F0.wireOp",EDGE,"E13.24.7"),sQuery(id+"F0.wireOp",EDGE,"E13.24.8"),sQuery(id+"F0.wireOp",EDGE,"E13.24.10"),sQuery(id+"F0.wireOp",EDGE,"E13.24.11"),sQuery(id+"F0.wireOp",EDGE,"E13.24.12"),sQuery(id+"F0.wireOp",EDGE,"E13.25.0"),sQuery(id+"F0.wireOp",EDGE,"E13.25.1"),sQuery(id+"F0.wireOp",EDGE,"E13.25.2"),sQuery(id+"F0.wireOp",EDGE,"E13.25.3"),sQuery(id+"F0.wireOp",EDGE,"E13.25.4"),sQuery(id+"F0.wireOp",EDGE,"E13.25.5"),sQuery(id+"F0.wireOp",EDGE,"E13.25.6"),sQuery(id+"F0.wireOp",EDGE,"E13.25.7"),sQuery(id+"F0.wireOp",EDGE,"E13.25.8"),sQuery(id+"F0.wireOp",EDGE,"E13.25.10"),sQuery(id+"F0.wireOp",EDGE,"E13.25.11"),sQuery(id+"F0.wireOp",EDGE,"E13.25.12"),sQuery(id+"F0.wireOp",EDGE,"E13.26.0"),sQuery(id+"F0.wireOp",EDGE,"E13.26.1"),sQuery(id+"F0.wireOp",EDGE,"E13.26.2"),sQuery(id+"F0.wireOp",EDGE,"E13.26.3"),sQuery(id+"F0.wireOp",EDGE,"E13.26.4"),sQuery(id+"F0.wireOp",EDGE,"E13.26.5"),sQuery(id+"F0.wireOp",EDGE,"E13.26.6"),sQuery(id+"F0.wireOp",EDGE,"E13.26.7"),sQuery(id+"F0.wireOp",EDGE,"E13.26.8"),sQuery(id+"F0.wireOp",EDGE,"E13.26.10"),sQuery(id+"F0.wireOp",EDGE,"E13.26.11"),sQuery(id+"F0.wireOp",EDGE,"E13.26.12"),sQuery(id+"F0.wireOp",EDGE,"E13.27.0"),sQuery(id+"F0.wireOp",EDGE,"E13.27.1"),sQuery(id+"F0.wireOp",EDGE,"E13.27.2"),sQuery(id+"F0.wireOp",EDGE,"E13.27.3"),sQuery(id+"F0.wireOp",EDGE,"E13.27.4"),sQuery(id+"F0.wireOp",EDGE,"E13.27.5"),sQuery(id+"F0.wireOp",EDGE,"E13.27.6"),sQuery(id+"F0.wireOp",EDGE,"E13.27.7"),sQuery(id+"F0.wireOp",EDGE,"E13.27.8"),sQuery(id+"F0.wireOp",EDGE,"E13.27.10"),sQuery(id+"F0.wireOp",EDGE,"E13.27.11"),sQuery(id+"F0.wireOp",EDGE,"E13.27.12"),sQuery(id+"F0.wireOp",EDGE,"E13.28.0"),sQuery(id+"F0.wireOp",EDGE,"E13.28.1"),sQuery(id+"F0.wireOp",EDGE,"E13.28.2"),sQuery(id+"F0.wireOp",EDGE,"E13.28.3"),sQuery(id+"F0.wireOp",EDGE,"E13.28.4"),sQuery(id+"F0.wireOp",EDGE,"E13.28.5"),sQuery(id+"F0.wireOp",EDGE,"E13.28.6"),sQuery(id+"F0.wireOp",EDGE,"E13.28.7"),sQuery(id+"F0.wireOp",EDGE,"E13.28.8"),sQuery(id+"F0.wireOp",EDGE,"E13.28.10"),sQuery(id+"F0.wireOp",EDGE,"E13.28.11"),sQuery(id+"F0.wireOp",EDGE,"E13.28.12"),sQuery(id+"F0.wireOp",EDGE,"E13.29.0"),sQuery(id+"F0.wireOp",EDGE,"E13.29.1"),sQuery(id+"F0.wireOp",EDGE,"E13.29.2"),sQuery(id+"F0.wireOp",EDGE,"E13.29.3"),sQuery(id+"F0.wireOp",EDGE,"E13.29.4"),sQuery(id+"F0.wireOp",EDGE,"E13.29.5"),sQuery(id+"F0.wireOp",EDGE,"E13.29.6"),sQuery(id+"F0.wireOp",EDGE,"E13.29.7"),sQuery(id+"F0.wireOp",EDGE,"E13.29.8"),sQuery(id+"F0.wireOp",EDGE,"E13.29.10"),sQuery(id+"F0.wireOp",EDGE,"E13.29.11"),sQuery(id+"F0.wireOp",EDGE,"E13.29.12"),sQuery(id+"F0.wireOp",EDGE,"E13.30.0"),sQuery(id+"F0.wireOp",EDGE,"E13.30.1"),sQuery(id+"F0.wireOp",EDGE,"E13.30.2"),sQuery(id+"F0.wireOp",EDGE,"E13.30.3"),sQuery(id+"F0.wireOp",EDGE,"E13.30.4"),sQuery(id+"F0.wireOp",EDGE,"E13.30.5"),sQuery(id+"F0.wireOp",EDGE,"E13.30.6"),sQuery(id+"F0.wireOp",EDGE,"E13.30.7"),sQuery(id+"F0.wireOp",EDGE,"E13.30.8"),sQuery(id+"F0.wireOp",EDGE,"E13.30.10"),sQuery(id+"F0.wireOp",EDGE,"E13.30.11"),sQuery(id+"F0.wireOp",EDGE,"E13.30.12"),sQuery(id+"F0.wireOp",EDGE,"E13.31.0"),sQuery(id+"F0.wireOp",EDGE,"E13.31.1"),sQuery(id+"F0.wireOp",EDGE,"E13.31.2"),sQuery(id+"F0.wireOp",EDGE,"E13.31.3"),sQuery(id+"F0.wireOp",EDGE,"E13.31.4"),sQuery(id+"F0.wireOp",EDGE,"E13.31.5"),sQuery(id+"F0.wireOp",EDGE,"E13.31.6"),sQuery(id+"F0.wireOp",EDGE,"E13.31.7"),sQuery(id+"F0.wireOp",EDGE,"E13.31.8"),sQuery(id+"F0.wireOp",EDGE,"E13.31.10"),sQuery(id+"F0.wireOp",EDGE,"E13.31.11"),sQuery(id+"F0.wireOp",EDGE,"E13.31.12"),sQuery(id+"F0.wireOp",EDGE,"E13.32.0"),sQuery(id+"F0.wireOp",EDGE,"E13.32.1"),sQuery(id+"F0.wireOp",EDGE,"E13.32.2"),sQuery(id+"F0.wireOp",EDGE,"E13.32.3"),sQuery(id+"F0.wireOp",EDGE,"E13.32.4"),sQuery(id+"F0.wireOp",EDGE,"E13.32.5"),sQuery(id+"F0.wireOp",EDGE,"E13.32.6"),sQuery(id+"F0.wireOp",EDGE,"E13.32.7"),sQuery(id+"F0.wireOp",EDGE,"E13.32.8"),sQuery(id+"F0.wireOp",EDGE,"E13.32.10"),sQuery(id+"F0.wireOp",EDGE,"E13.32.11"),sQuery(id+"F0.wireOp",EDGE,"E13.32.12"),sQuery(id+"F0.wireOp",EDGE,"E13.33.0"),sQuery(id+"F0.wireOp",EDGE,"E13.33.1"),sQuery(id+"F0.wireOp",EDGE,"E13.33.2"),sQuery(id+"F0.wireOp",EDGE,"E13.33.3"),sQuery(id+"F0.wireOp",EDGE,"E13.33.4"),sQuery(id+"F0.wireOp",EDGE,"E13.33.5"),sQuery(id+"F0.wireOp",EDGE,"E13.33.6"),sQuery(id+"F0.wireOp",EDGE,"E13.33.7"),sQuery(id+"F0.wireOp",EDGE,"E13.33.8"),sQuery(id+"F0.wireOp",EDGE,"E13.33.10"),sQuery(id+"F0.wireOp",EDGE,"E13.33.11"),sQuery(id+"F0.wireOp",EDGE,"E13.33.12"),sQuery(id+"F0.wireOp",EDGE,"E13.34.0"),sQuery(id+"F0.wireOp",EDGE,"E13.34.1"),sQuery(id+"F0.wireOp",EDGE,"E13.34.2"),sQuery(id+"F0.wireOp",EDGE,"E13.34.3"),sQuery(id+"F0.wireOp",EDGE,"E13.34.4"),sQuery(id+"F0.wireOp",EDGE,"E13.34.5"),sQuery(id+"F0.wireOp",EDGE,"E13.34.6"),sQuery(id+"F0.wireOp",EDGE,"E13.34.7"),sQuery(id+"F0.wireOp",EDGE,"E13.34.8"),sQuery(id+"F0.wireOp",EDGE,"E13.34.10"),sQuery(id+"F0.wireOp",EDGE,"E13.34.11"),sQuery(id+"F0.wireOp",EDGE,"E13.34.12"),sQuery(id+"F0.wireOp",EDGE,"E13.35.0"),sQuery(id+"F0.wireOp",EDGE,"E13.35.1"),sQuery(id+"F0.wireOp",EDGE,"E13.35.2"),sQuery(id+"F0.wireOp",EDGE,"E13.35.3"),sQuery(id+"F0.wireOp",EDGE,"E13.35.4"),sQuery(id+"F0.wireOp",EDGE,"E13.35.5"),sQuery(id+"F0.wireOp",EDGE,"E13.35.6"),sQuery(id+"F0.wireOp",EDGE,"E13.35.7"),sQuery(id+"F0.wireOp",EDGE,"E13.35.8"),sQuery(id+"F0.wireOp",EDGE,"E13.35.10"),sQuery(id+"F0.wireOp",EDGE,"E13.35.11"),sQuery(id+"F0.wireOp",EDGE,"E13.35.12"),sQuery(id+"F0.wireOp",EDGE,"E13.36.0"),sQuery(id+"F0.wireOp",EDGE,"E13.36.1"),sQuery(id+"F0.wireOp",EDGE,"E13.36.2"),sQuery(id+"F0.wireOp",EDGE,"E13.36.3"),sQuery(id+"F0.wireOp",EDGE,"E13.36.4"),sQuery(id+"F0.wireOp",EDGE,"E13.36.5"),sQuery(id+"F0.wireOp",EDGE,"E13.36.6"),sQuery(id+"F0.wireOp",EDGE,"E13.36.7"),sQuery(id+"F0.wireOp",EDGE,"E13.36.8"),sQuery(id+"F0.wireOp",EDGE,"E13.36.10"),sQuery(id+"F0.wireOp",EDGE,"E13.36.11"),sQuery(id+"F0.wireOp",EDGE,"E13.36.12"),sQuery(id+"F0.wireOp",EDGE,"E13.37.0"),sQuery(id+"F0.wireOp",EDGE,"E13.37.1"),sQuery(id+"F0.wireOp",EDGE,"E13.37.2"),sQuery(id+"F0.wireOp",EDGE,"E13.37.3"),sQuery(id+"F0.wireOp",EDGE,"E13.37.4"),sQuery(id+"F0.wireOp",EDGE,"E13.37.5"),sQuery(id+"F0.wireOp",EDGE,"E13.37.6"),sQuery(id+"F0.wireOp",EDGE,"E13.37.7"),sQuery(id+"F0.wireOp",EDGE,"E13.37.8"),sQuery(id+"F0.wireOp",EDGE,"E13.37.10"),sQuery(id+"F0.wireOp",EDGE,"E13.37.11"),sQuery(id+"F0.wireOp",EDGE,"E13.37.12"),sQuery(id+"F0.wireOp",EDGE,"E13.38.0"),sQuery(id+"F0.wireOp",EDGE,"E13.38.1"),sQuery(id+"F0.wireOp",EDGE,"E13.38.2"),sQuery(id+"F0.wireOp",EDGE,"E13.38.3"),sQuery(id+"F0.wireOp",EDGE,"E13.38.4"),sQuery(id+"F0.wireOp",EDGE,"E13.38.5"),sQuery(id+"F0.wireOp",EDGE,"E13.38.6"),sQuery(id+"F0.wireOp",EDGE,"E13.38.7"),sQuery(id+"F0.wireOp",EDGE,"E13.38.8"),sQuery(id+"F0.wireOp",EDGE,"E13.38.10"),sQuery(id+"F0.wireOp",EDGE,"E13.38.11"),sQuery(id+"F0.wireOp",EDGE,"E13.38.12"),sQuery(id+"F0.wireOp",EDGE,"E13.39.0"),sQuery(id+"F0.wireOp",EDGE,"E13.39.1"),sQuery(id+"F0.wireOp",EDGE,"E13.39.2"),sQuery(id+"F0.wireOp",EDGE,"E13.39.3"),sQuery(id+"F0.wireOp",EDGE,"E13.39.4"),sQuery(id+"F0.wireOp",EDGE,"E13.39.5"),sQuery(id+"F0.wireOp",EDGE,"E13.39.6"),sQuery(id+"F0.wireOp",EDGE,"E13.39.7"),sQuery(id+"F0.wireOp",EDGE,"E13.39.8"),sQuery(id+"F0.wireOp",EDGE,"E13.39.10"),sQuery(id+"F0.wireOp",EDGE,"E13.39.11"),sQuery(id+"F0.wireOp",EDGE,"E13.39.12"),sQuery(id+"F0.wireOp",EDGE,"E13.40.0"),sQuery(id+"F0.wireOp",EDGE,"E13.40.1"),sQuery(id+"F0.wireOp",EDGE,"E13.40.2"),sQuery(id+"F0.wireOp",EDGE,"E13.40.3"),sQuery(id+"F0.wireOp",EDGE,"E13.40.4"),sQuery(id+"F0.wireOp",EDGE,"E13.40.5"),sQuery(id+"F0.wireOp",EDGE,"E13.40.6"),sQuery(id+"F0.wireOp",EDGE,"E13.40.7"),sQuery(id+"F0.wireOp",EDGE,"E13.40.8"),sQuery(id+"F0.wireOp",EDGE,"E13.40.10"),sQuery(id+"F0.wireOp",EDGE,"E13.40.11"),sQuery(id+"F0.wireOp",EDGE,"E13.40.12"),sQuery(id+"F0.wireOp",EDGE,"E13.41.0"),sQuery(id+"F0.wireOp",EDGE,"E13.41.1"),sQuery(id+"F0.wireOp",EDGE,"E13.41.2"),sQuery(id+"F0.wireOp",EDGE,"E13.41.3"),sQuery(id+"F0.wireOp",EDGE,"E13.41.4"),sQuery(id+"F0.wireOp",EDGE,"E13.41.5"),sQuery(id+"F0.wireOp",EDGE,"E13.41.6"),sQuery(id+"F0.wireOp",EDGE,"E13.41.7"),sQuery(id+"F0.wireOp",EDGE,"E13.41.8"),sQuery(id+"F0.wireOp",EDGE,"E13.41.10"),sQuery(id+"F0.wireOp",EDGE,"E13.41.11"),sQuery(id+"F0.wireOp",EDGE,"E13.41.12"),sQuery(id+"F0.wireOp",EDGE,"E13.42.0"),sQuery(id+"F0.wireOp",EDGE,"E13.42.1"),sQuery(id+"F0.wireOp",EDGE,"E13.42.2"),sQuery(id+"F0.wireOp",EDGE,"E13.42.3"),sQuery(id+"F0.wireOp",EDGE,"E13.42.4"),sQuery(id+"F0.wireOp",EDGE,"E13.42.5"),sQuery(id+"F0.wireOp",EDGE,"E13.42.6"),sQuery(id+"F0.wireOp",EDGE,"E13.42.7"),sQuery(id+"F0.wireOp",EDGE,"E13.42.8"),sQuery(id+"F0.wireOp",EDGE,"E13.42.10"),sQuery(id+"F0.wireOp",EDGE,"E13.42.11"),sQuery(id+"F0.wireOp",EDGE,"E13.42.12"),sQuery(id+"F0.wireOp",EDGE,"E13.43.0"),sQuery(id+"F0.wireOp",EDGE,"E13.43.1"),sQuery(id+"F0.wireOp",EDGE,"E13.43.2"),sQuery(id+"F0.wireOp",EDGE,"E13.43.3"),sQuery(id+"F0.wireOp",EDGE,"E13.43.4"),sQuery(id+"F0.wireOp",EDGE,"E13.43.5"),sQuery(id+"F0.wireOp",EDGE,"E13.43.6"),sQuery(id+"F0.wireOp",EDGE,"E13.43.7"),sQuery(id+"F0.wireOp",EDGE,"E13.43.8"),sQuery(id+"F0.wireOp",EDGE,"E13.43.10"),sQuery(id+"F0.wireOp",EDGE,"E13.43.11"),sQuery(id+"F0.wireOp",EDGE,"E13.43.12"),sQuery(id+"F0.wireOp",EDGE,"E13.44.0"),sQuery(id+"F0.wireOp",EDGE,"E13.44.1"),sQuery(id+"F0.wireOp",EDGE,"E13.44.2"),sQuery(id+"F0.wireOp",EDGE,"E13.44.3"),sQuery(id+"F0.wireOp",EDGE,"E13.44.4"),sQuery(id+"F0.wireOp",EDGE,"E13.44.5"),sQuery(id+"F0.wireOp",EDGE,"E13.44.6"),sQuery(id+"F0.wireOp",EDGE,"E13.44.7"),sQuery(id+"F0.wireOp",EDGE,"E13.44.8"),sQuery(id+"F0.wireOp",EDGE,"E13.44.10"),sQuery(id+"F0.wireOp",EDGE,"E13.44.11"),sQuery(id+"F0.wireOp",EDGE,"E13.44.12"),sQuery(id+"F0.wireOp",EDGE,"E13.45.0"),sQuery(id+"F0.wireOp",EDGE,"E13.45.1"),sQuery(id+"F0.wireOp",EDGE,"E13.45.2"),sQuery(id+"F0.wireOp",EDGE,"E13.45.3"),sQuery(id+"F0.wireOp",EDGE,"E13.45.4"),sQuery(id+"F0.wireOp",EDGE,"E13.45.5"),sQuery(id+"F0.wireOp",EDGE,"E13.45.6"),sQuery(id+"F0.wireOp",EDGE,"E13.45.7"),sQuery(id+"F0.wireOp",EDGE,"E13.45.8"),sQuery(id+"F0.wireOp",EDGE,"E13.45.10"),sQuery(id+"F0.wireOp",EDGE,"E13.45.11"),sQuery(id+"F0.wireOp",EDGE,"E13.45.12"),sQuery(id+"F0.wireOp",EDGE,"E13.46.0"),sQuery(id+"F0.wireOp",EDGE,"E13.46.1"),sQuery(id+"F0.wireOp",EDGE,"E13.46.2"),sQuery(id+"F0.wireOp",EDGE,"E13.46.3"),sQuery(id+"F0.wireOp",EDGE,"E13.46.4"),sQuery(id+"F0.wireOp",EDGE,"E13.46.5"),sQuery(id+"F0.wireOp",EDGE,"E13.46.6"),sQuery(id+"F0.wireOp",EDGE,"E13.46.7"),sQuery(id+"F0.wireOp",EDGE,"E13.46.8"),sQuery(id+"F0.wireOp",EDGE,"E13.46.10"),sQuery(id+"F0.wireOp",EDGE,"E13.46.11"),sQuery(id+"F0.wireOp",EDGE,"E13.46.12"),sQuery(id+"F0.wireOp",EDGE,"E13.47.0"),sQuery(id+"F0.wireOp",EDGE,"E13.47.1"),sQuery(id+"F0.wireOp",EDGE,"E13.47.2"),sQuery(id+"F0.wireOp",EDGE,"E13.47.3"),sQuery(id+"F0.wireOp",EDGE,"E13.47.4"),sQuery(id+"F0.wireOp",EDGE,"E13.47.5"),sQuery(id+"F0.wireOp",EDGE,"E13.47.6"),sQuery(id+"F0.wireOp",EDGE,"E13.47.7"),sQuery(id+"F0.wireOp",EDGE,"E13.47.8"),sQuery(id+"F0.wireOp",EDGE,"E13.47.10"),sQuery(id+"F0.wireOp",EDGE,"E13.47.11"),sQuery(id+"F0.wireOp",EDGE,"E13.47.12"),sQuery(id+"F0.wireOp",EDGE,"E13.48.0"),sQuery(id+"F0.wireOp",EDGE,"E13.48.1"),sQuery(id+"F0.wireOp",EDGE,"E13.48.2"),sQuery(id+"F0.wireOp",EDGE,"E13.48.3"),sQuery(id+"F0.wireOp",EDGE,"E13.48.4"),sQuery(id+"F0.wireOp",EDGE,"E13.48.5"),sQuery(id+"F0.wireOp",EDGE,"E13.48.6"),sQuery(id+"F0.wireOp",EDGE,"E13.48.7"),sQuery(id+"F0.wireOp",EDGE,"E13.48.8"),sQuery(id+"F0.wireOp",EDGE,"E13.48.10"),sQuery(id+"F0.wireOp",EDGE,"E13.48.11"),sQuery(id+"F0.wireOp",EDGE,"E13.48.12"),sQuery(id+"F0.wireOp",EDGE,"E13.49.0"),sQuery(id+"F0.wireOp",EDGE,"E13.49.1"),sQuery(id+"F0.wireOp",EDGE,"E13.49.2"),sQuery(id+"F0.wireOp",EDGE,"E13.49.3"),sQuery(id+"F0.wireOp",EDGE,"E13.49.4"),sQuery(id+"F0.wireOp",EDGE,"E13.49.5"),sQuery(id+"F0.wireOp",EDGE,"E13.49.6"),sQuery(id+"F0.wireOp",EDGE,"E13.49.7"),sQuery(id+"F0.wireOp",EDGE,"E13.49.8"),sQuery(id+"F0.wireOp",EDGE,"E13.49.10"),sQuery(id+"F0.wireOp",EDGE,"E13.49.11"),sQuery(id+"F0.wireOp",EDGE,"E13.49.12"),sQuery(id+"F0.wireOp",EDGE,"E14.trimOffspring"),sQuery(id+"F0.wireOp",EDGE,"E15.trimOffspring"),sQuery(id+"F0.wireOp",EDGE,"E16.trimOffspring"),sQuery(id+"F0.wireOp",EDGE,"E17.trimOffspring"),sQuery(id+"F0.wireOp",EDGE,"E18.trimOffspring"),sQuery(id+"F0.wireOp",EDGE,"E19.trimOffspring"),sQuery(id+"F0.wireOp",EDGE,"E20.trimOffspring"),sQuery(id+"F0.wireOp",EDGE,"E21.trimOffspring"),sQuery(id+"F0.wireOp",EDGE,"E22.trimOffspring"),sQuery(id+"F0.wireOp",EDGE,"E23.trimOffspring"),sQuery(id+"F0.wireOp",EDGE,"E24.trimOffspring"),sQuery(id+"F0.wireOp",EDGE,"E25.trimOffspring"),sQuery(id+"F0.wireOp",EDGE,"E26.trimOffspring"),sQuery(id+"F0.wireOp",EDGE,"E27.trimOffspring"),sQuery(id+"F0.wireOp",EDGE,"E28.trimOffspring"),sQuery(id+"F0.wireOp",EDGE,"E29.trimOffspring"),sQuery(id+"F0.wireOp",EDGE,"E30.trimOffspring"),sQuery(id+"F0.wireOp",EDGE,"E31.trimOffspring"),sQuery(id+"F0.wireOp",EDGE,"E32.trimOffspring"),sQuery(id+"F0.wireOp",EDGE,"E33.trimOffspring"),sQuery(id+"F0.wireOp",EDGE,"E34.trimOffspring"),sQuery(id+"F0.wireOp",EDGE,"E35.trimOffspring"),sQuery(id+"F0.wireOp",EDGE,"E36.trimOffspring"),sQuery(id+"F0.wireOp",EDGE,"E37.trimOffspring"),sQuery(id+"F0.wireOp",EDGE,"E38.trimOffspring"),sQuery(id+"F0.wireOp",EDGE,"E39.trimOffspring"),sQuery(id+"F0.wireOp",EDGE,"E40.trimOffspring"),sQuery(id+"F0.wireOp",EDGE,"E41.trimOffspring"),sQuery(id+"F0.wireOp",EDGE,"E42.trimOffspring"),sQuery(id+"F0.wireOp",EDGE,"E43.trimOffspring"),sQuery(id+"F0.wireOp",EDGE,"E44.trimOffspring"),sQuery(id+"F0.wireOp",EDGE,"E45.trimOffspring"),sQuery(id+"F0.wireOp",EDGE,"E46.trimOffspring"),sQuery(id+"F0.wireOp",EDGE,"E47.trimOffspring"),sQuery(id+"F0.wireOp",EDGE,"E48.trimOffspring"),sQuery(id+"F0.wireOp",EDGE,"E49.trimOffspring"),sQuery(id+"F0.wireOp",EDGE,"E50.trimOffspring"),sQuery(id+"F0.wireOp",EDGE,"E51.trimOffspring"),sQuery(id+"F0.wireOp",EDGE,"E52.trimOffspring"),sQuery(id+"F0.wireOp",EDGE,"E53.trimOffspring"),sQuery(id+"F0.wireOp",EDGE,"E54.trimOffspring"),sQuery(id+"F0.wireOp",EDGE,"E55.trimOffspring"),sQuery(id+"F0.wireOp",EDGE,"E56.trimOffspring"),sQuery(id+"F0.wireOp",EDGE,"E57.trimOffspring"),sQuery(id+"F0.wireOp",EDGE,"E58.trimOffspring"),sQuery(id+"F0.wireOp",EDGE,"E59.trimOffspring"),sQuery(id+"F0.wireOp",EDGE,"E60.trimOffspring"),sQuery(id+"F0.wireOp",EDGE,"E61.trimOffspring"),sQuery(id+"F0.wireOp",EDGE,"E62"),sQuery(id+"F0.wireOp",EDGE,"E63")])],"isStart":false});
            var sketch = newSketch(context, id + "F2", { "sketchPlane" : qUnion([Q0])});
            skArc(sketch, "E64", {"start": v(-0.12, 76.5) * mm, "mid": v(-1.26, 78.85) * mm, "end": v(-2.72, 81.02) * mm});
            skArc(sketch, "E65.0", {"start": v(0, 71.12) * mm, "mid": v(-3.72, 71.02) * mm, "end": v(-7.43, 70.73) * mm});
            skLineSegment(sketch, "E66", {"start": v(0, 75.9) * mm, "end": v(0, 71.12) * mm});
            skLineSegment(sketch, "E67", {"start": v(-3.14, 81.22) * mm, "end": v(-4.25, 81.18) * mm});
            skLineSegment(sketch, "E68.MirrorCS", {"start": v(-5.37, 81.1) * mm, "end": v(-4.25, 81.18) * mm});
            skArc(sketch, "E69.MirrorCS", {"start": v(-7.88, 76.09) * mm, "mid": v(-6.99, 78.55) * mm, "end": v(-5.77, 80.86) * mm});
            skLineSegment(sketch, "E70.MirrorCS", {"start": v(-7.93, 75.48) * mm, "end": v(-7.43, 70.73) * mm});
            skPoint(sketch, "E71.visualSharp", {"position": v(0, 76.2) * mm});
            skArc(sketch, "E71.filletArc", {"start": v(0, 75.9) * mm, "mid": v(-0.03, 76.2) * mm, "end": v(-0.12, 76.5) * mm});
            skPoint(sketch, "E72.visualSharp", {"position": v(-7.97, 75.78) * mm});
            skArc(sketch, "E72.filletArc", {"start": v(-7.88, 76.09) * mm, "mid": v(-7.94, 75.79) * mm, "end": v(-7.93, 75.48) * mm});
            skPoint(sketch, "E73.visualSharp", {"position": v(-5.63, 81.08) * mm});
            skArc(sketch, "E73.filletArc", {"start": v(-5.37, 81.1) * mm, "mid": v(-5.6, 81.03) * mm, "end": v(-5.77, 80.86) * mm});
            skPoint(sketch, "E74.visualSharp", {"position": v(-2.88, 81.23) * mm});
            skArc(sketch, "E74.filletArc", {"start": v(-2.72, 81.02) * mm, "mid": v(-2.9, 81.17) * mm, "end": v(-3.14, 81.22) * mm});
            skSolve(sketch);
        }
        {
            var Q0;
            Q0=makeQuery(id+"F2.imprint","IMPRINT",FACE,{"disambiguationData":[TD([[makeQuery(id+"F2.imprint","IMPRINT",EDGE,{"derivedFrom":sQuery(id+"F2.wireOp",EDGE,"E64")}),1.0]])]});
            extrude(context, id + "F3", {"entities" : qUnion([Q0]), "oppositeDirection" : true, "depth" : 127 * mm});
        }
        {
            var Q0;
            Q0=makeQuery(id+"F3.opExtrude","SWEPT_BODY",BODY,{"disambiguationData":[OSD([sQuery(id+"F2.wireOp",EDGE,"E64"),sQuery(id+"F2.wireOp",EDGE,"E65.0"),sQuery(id+"F2.wireOp",EDGE,"E66"),sQuery(id+"F2.wireOp",EDGE,"E67"),sQuery(id+"F2.wireOp",EDGE,"E68.MirrorCS"),sQuery(id+"F2.wireOp",EDGE,"E69.MirrorCS"),sQuery(id+"F2.wireOp",EDGE,"E70.MirrorCS"),sQuery(id+"F2.wireOp",EDGE,"E71.filletArc"),sQuery(id+"F2.wireOp",EDGE,"E72.filletArc"),sQuery(id+"F2.wireOp",EDGE,"E73.filletArc"),sQuery(id+"F2.wireOp",EDGE,"E74.filletArc")])]});
            var Q1;
            Q1=makeQuery(id+"F1.opExtrude","CAP_EDGE",EDGE,{"disambiguationData":[OSD([sQuery(id+"F0.wireOp",EDGE,"E62")])],"isStart":false});
            circularPattern(context, id + "F4", {"entities" : qUnion([Q0]), "axis" : qUnion([Q1]), "angle" : 360 * degree, "instanceCount" : 30, "equalSpace" : true});
        }
        {
            var Q0;
            Q0=makeQuery(id+"F3.opExtrude","SWEPT_EDGE",EDGE,{"disambiguationData":[OSD([sQuery(id+"F0.wireOp",EDGE,"E62"),sQuery(id+"F2.wireOp",EDGE,"E65.0"),sQuery(id+"F2.wireOp",EDGE,"E66")])]});
            var Q1;
            Q1=makeQuery(id+"F4.opPattern","COPY",EDGE,{"derivedFrom":makeQuery(id+"F3.opExtrude","SWEPT_EDGE",EDGE,{"disambiguationData":[OSD([sQuery(id+"F0.wireOp",EDGE,"E62"),sQuery(id+"F2.wireOp",EDGE,"E65.0"),sQuery(id+"F2.wireOp",EDGE,"E66")])]}),"instanceName":"29"});
            var Q2;
            Q2=makeQuery(id+"F4.opPattern","COPY",EDGE,{"derivedFrom":makeQuery(id+"F3.opExtrude","SWEPT_EDGE",EDGE,{"disambiguationData":[OSD([sQuery(id+"F0.wireOp",EDGE,"E62"),sQuery(id+"F2.wireOp",EDGE,"E65.0"),sQuery(id+"F2.wireOp",EDGE,"E66")])]}),"instanceName":"27"});
            var Q3;
            Q3=makeQuery(id+"F4.opPattern","COPY",EDGE,{"derivedFrom":makeQuery(id+"F3.opExtrude","SWEPT_EDGE",EDGE,{"disambiguationData":[OSD([sQuery(id+"F0.wireOp",EDGE,"E62"),sQuery(id+"F2.wireOp",EDGE,"E65.0"),sQuery(id+"F2.wireOp",EDGE,"E66")])]}),"instanceName":"28"});
            var Q4;
            Q4=makeQuery(id+"F4.opPattern","COPY",EDGE,{"derivedFrom":makeQuery(id+"F3.opExtrude","SWEPT_EDGE",EDGE,{"disambiguationData":[OSD([sQuery(id+"F0.wireOp",EDGE,"E62"),sQuery(id+"F2.wireOp",EDGE,"E65.0"),sQuery(id+"F2.wireOp",EDGE,"E66")])]}),"instanceName":"26"});
            var Q5;
            Q5=makeQuery(id+"F4.opPattern","COPY",EDGE,{"derivedFrom":makeQuery(id+"F3.opExtrude","SWEPT_EDGE",EDGE,{"disambiguationData":[OSD([sQuery(id+"F0.wireOp",EDGE,"E62"),sQuery(id+"F2.wireOp",EDGE,"E65.0"),sQuery(id+"F2.wireOp",EDGE,"E66")])]}),"instanceName":"24"});
            var Q6;
            Q6=makeQuery(id+"F4.opPattern","COPY",EDGE,{"derivedFrom":makeQuery(id+"F3.opExtrude","SWEPT_EDGE",EDGE,{"disambiguationData":[OSD([sQuery(id+"F0.wireOp",EDGE,"E62"),sQuery(id+"F2.wireOp",EDGE,"E65.0"),sQuery(id+"F2.wireOp",EDGE,"E66")])]}),"instanceName":"22"});
            var Q7;
            Q7=makeQuery(id+"F4.opPattern","COPY",EDGE,{"derivedFrom":makeQuery(id+"F3.opExtrude","SWEPT_EDGE",EDGE,{"disambiguationData":[OSD([sQuery(id+"F0.wireOp",EDGE,"E62"),sQuery(id+"F2.wireOp",EDGE,"E65.0"),sQuery(id+"F2.wireOp",EDGE,"E66")])]}),"instanceName":"21"});
            var Q8;
            Q8=makeQuery(id+"F4.opPattern","COPY",EDGE,{"derivedFrom":makeQuery(id+"F3.opExtrude","SWEPT_EDGE",EDGE,{"disambiguationData":[OSD([sQuery(id+"F0.wireOp",EDGE,"E62"),sQuery(id+"F2.wireOp",EDGE,"E65.0"),sQuery(id+"F2.wireOp",EDGE,"E66")])]}),"instanceName":"20"});
            var Q9;
            Q9=makeQuery(id+"F4.opPattern","COPY",EDGE,{"derivedFrom":makeQuery(id+"F3.opExtrude","SWEPT_EDGE",EDGE,{"disambiguationData":[OSD([sQuery(id+"F0.wireOp",EDGE,"E62"),sQuery(id+"F2.wireOp",EDGE,"E65.0"),sQuery(id+"F2.wireOp",EDGE,"E66")])]}),"instanceName":"19"});
            var Q10;
            Q10=makeQuery(id+"F4.opPattern","COPY",EDGE,{"derivedFrom":makeQuery(id+"F3.opExtrude","SWEPT_EDGE",EDGE,{"disambiguationData":[OSD([sQuery(id+"F0.wireOp",EDGE,"E62"),sQuery(id+"F2.wireOp",EDGE,"E65.0"),sQuery(id+"F2.wireOp",EDGE,"E66")])]}),"instanceName":"18"});
            var Q11;
            Q11=makeQuery(id+"F4.opPattern","COPY",EDGE,{"derivedFrom":makeQuery(id+"F3.opExtrude","SWEPT_EDGE",EDGE,{"disambiguationData":[OSD([sQuery(id+"F0.wireOp",EDGE,"E62"),sQuery(id+"F2.wireOp",EDGE,"E65.0"),sQuery(id+"F2.wireOp",EDGE,"E66")])]}),"instanceName":"17"});
            var Q12;
            Q12=makeQuery(id+"F4.opPattern","COPY",EDGE,{"derivedFrom":makeQuery(id+"F3.opExtrude","SWEPT_EDGE",EDGE,{"disambiguationData":[OSD([sQuery(id+"F0.wireOp",EDGE,"E62"),sQuery(id+"F2.wireOp",EDGE,"E65.0"),sQuery(id+"F2.wireOp",EDGE,"E66")])]}),"instanceName":"16"});
            var Q13;
            Q13=makeQuery(id+"F4.opPattern","COPY",EDGE,{"derivedFrom":makeQuery(id+"F3.opExtrude","SWEPT_EDGE",EDGE,{"disambiguationData":[OSD([sQuery(id+"F0.wireOp",EDGE,"E62"),sQuery(id+"F2.wireOp",EDGE,"E65.0"),sQuery(id+"F2.wireOp",EDGE,"E66")])]}),"instanceName":"15"});
            var Q14;
            Q14=makeQuery(id+"F4.opPattern","COPY",EDGE,{"derivedFrom":makeQuery(id+"F3.opExtrude","SWEPT_EDGE",EDGE,{"disambiguationData":[OSD([sQuery(id+"F0.wireOp",EDGE,"E62"),sQuery(id+"F2.wireOp",EDGE,"E65.0"),sQuery(id+"F2.wireOp",EDGE,"E66")])]}),"instanceName":"14"});
            var Q15;
            Q15=makeQuery(id+"F4.opPattern","COPY",EDGE,{"derivedFrom":makeQuery(id+"F3.opExtrude","SWEPT_EDGE",EDGE,{"disambiguationData":[OSD([sQuery(id+"F0.wireOp",EDGE,"E62"),sQuery(id+"F2.wireOp",EDGE,"E65.0"),sQuery(id+"F2.wireOp",EDGE,"E66")])]}),"instanceName":"13"});
            var Q16;
            Q16=makeQuery(id+"F4.opPattern","COPY",EDGE,{"derivedFrom":makeQuery(id+"F3.opExtrude","SWEPT_EDGE",EDGE,{"disambiguationData":[OSD([sQuery(id+"F0.wireOp",EDGE,"E62"),sQuery(id+"F2.wireOp",EDGE,"E65.0"),sQuery(id+"F2.wireOp",EDGE,"E66")])]}),"instanceName":"12"});
            var Q17;
            Q17=makeQuery(id+"F4.opPattern","COPY",EDGE,{"derivedFrom":makeQuery(id+"F3.opExtrude","SWEPT_EDGE",EDGE,{"disambiguationData":[OSD([sQuery(id+"F0.wireOp",EDGE,"E62"),sQuery(id+"F2.wireOp",EDGE,"E65.0"),sQuery(id+"F2.wireOp",EDGE,"E66")])]}),"instanceName":"11"});
            var Q18;
            Q18=makeQuery(id+"F4.opPattern","COPY",EDGE,{"derivedFrom":makeQuery(id+"F3.opExtrude","SWEPT_EDGE",EDGE,{"disambiguationData":[OSD([sQuery(id+"F0.wireOp",EDGE,"E62"),sQuery(id+"F2.wireOp",EDGE,"E65.0"),sQuery(id+"F2.wireOp",EDGE,"E66")])]}),"instanceName":"10"});
            var Q19;
            Q19=makeQuery(id+"F4.opPattern","COPY",EDGE,{"derivedFrom":makeQuery(id+"F3.opExtrude","SWEPT_EDGE",EDGE,{"disambiguationData":[OSD([sQuery(id+"F0.wireOp",EDGE,"E62"),sQuery(id+"F2.wireOp",EDGE,"E65.0"),sQuery(id+"F2.wireOp",EDGE,"E66")])]}),"instanceName":"9"});
            var Q20;
            Q20=makeQuery(id+"F4.opPattern","COPY",EDGE,{"derivedFrom":makeQuery(id+"F3.opExtrude","SWEPT_EDGE",EDGE,{"disambiguationData":[OSD([sQuery(id+"F0.wireOp",EDGE,"E62"),sQuery(id+"F2.wireOp",EDGE,"E65.0"),sQuery(id+"F2.wireOp",EDGE,"E66")])]}),"instanceName":"8"});
            var Q21;
            Q21=makeQuery(id+"F4.opPattern","COPY",EDGE,{"derivedFrom":makeQuery(id+"F3.opExtrude","SWEPT_EDGE",EDGE,{"disambiguationData":[OSD([sQuery(id+"F0.wireOp",EDGE,"E62"),sQuery(id+"F2.wireOp",EDGE,"E65.0"),sQuery(id+"F2.wireOp",EDGE,"E66")])]}),"instanceName":"7"});
            var Q22;
            Q22=makeQuery(id+"F4.opPattern","COPY",EDGE,{"derivedFrom":makeQuery(id+"F3.opExtrude","SWEPT_EDGE",EDGE,{"disambiguationData":[OSD([sQuery(id+"F0.wireOp",EDGE,"E62"),sQuery(id+"F2.wireOp",EDGE,"E65.0"),sQuery(id+"F2.wireOp",EDGE,"E66")])]}),"instanceName":"6"});
            var Q23;
            Q23=makeQuery(id+"F4.opPattern","COPY",EDGE,{"derivedFrom":makeQuery(id+"F3.opExtrude","SWEPT_EDGE",EDGE,{"disambiguationData":[OSD([sQuery(id+"F0.wireOp",EDGE,"E62"),sQuery(id+"F2.wireOp",EDGE,"E65.0"),sQuery(id+"F2.wireOp",EDGE,"E66")])]}),"instanceName":"4"});
            var Q24;
            Q24=makeQuery(id+"F4.opPattern","COPY",EDGE,{"derivedFrom":makeQuery(id+"F3.opExtrude","SWEPT_EDGE",EDGE,{"disambiguationData":[OSD([sQuery(id+"F0.wireOp",EDGE,"E62"),sQuery(id+"F2.wireOp",EDGE,"E65.0"),sQuery(id+"F2.wireOp",EDGE,"E66")])]}),"instanceName":"3"});
            var Q25;
            Q25=makeQuery(id+"F4.opPattern","COPY",EDGE,{"derivedFrom":makeQuery(id+"F3.opExtrude","SWEPT_EDGE",EDGE,{"disambiguationData":[OSD([sQuery(id+"F0.wireOp",EDGE,"E62"),sQuery(id+"F2.wireOp",EDGE,"E65.0"),sQuery(id+"F2.wireOp",EDGE,"E66")])]}),"instanceName":"2"});
            var Q26;
            Q26=makeQuery(id+"F4.opPattern","COPY",EDGE,{"derivedFrom":makeQuery(id+"F3.opExtrude","SWEPT_EDGE",EDGE,{"disambiguationData":[OSD([sQuery(id+"F0.wireOp",EDGE,"E62"),sQuery(id+"F2.wireOp",EDGE,"E65.0"),sQuery(id+"F2.wireOp",EDGE,"E66")])]}),"instanceName":"1"});
            var Q27;
            Q27=makeQuery(id+"F4.opPattern","COPY",EDGE,{"derivedFrom":makeQuery(id+"F3.opExtrude","SWEPT_EDGE",EDGE,{"disambiguationData":[OSD([sQuery(id+"F0.wireOp",EDGE,"E62"),sQuery(id+"F2.wireOp",EDGE,"E65.0"),sQuery(id+"F2.wireOp",EDGE,"E66")])]}),"instanceName":"5"});
            var Q28;
            Q28=makeQuery(id+"F4.opPattern","COPY",EDGE,{"derivedFrom":makeQuery(id+"F3.opExtrude","SWEPT_EDGE",EDGE,{"disambiguationData":[OSD([sQuery(id+"F0.wireOp",EDGE,"E62"),sQuery(id+"F2.wireOp",EDGE,"E65.0"),sQuery(id+"F2.wireOp",EDGE,"E70.MirrorCS")])]}),"instanceName":"2"});
            var Q29;
            Q29=makeQuery(id+"F4.opPattern","COPY",EDGE,{"derivedFrom":makeQuery(id+"F3.opExtrude","SWEPT_EDGE",EDGE,{"disambiguationData":[OSD([sQuery(id+"F0.wireOp",EDGE,"E62"),sQuery(id+"F2.wireOp",EDGE,"E65.0"),sQuery(id+"F2.wireOp",EDGE,"E70.MirrorCS")])]}),"instanceName":"1"});
            var Q30;
            Q30=makeQuery(id+"F3.opExtrude","SWEPT_EDGE",EDGE,{"disambiguationData":[OSD([sQuery(id+"F0.wireOp",EDGE,"E62"),sQuery(id+"F2.wireOp",EDGE,"E65.0"),sQuery(id+"F2.wireOp",EDGE,"E70.MirrorCS")])]});
            var Q31;
            Q31=makeQuery(id+"F4.opPattern","COPY",EDGE,{"derivedFrom":makeQuery(id+"F3.opExtrude","SWEPT_EDGE",EDGE,{"disambiguationData":[OSD([sQuery(id+"F0.wireOp",EDGE,"E62"),sQuery(id+"F2.wireOp",EDGE,"E65.0"),sQuery(id+"F2.wireOp",EDGE,"E70.MirrorCS")])]}),"instanceName":"29"});
            var Q32;
            Q32=makeQuery(id+"F4.opPattern","COPY",EDGE,{"derivedFrom":makeQuery(id+"F3.opExtrude","SWEPT_EDGE",EDGE,{"disambiguationData":[OSD([sQuery(id+"F0.wireOp",EDGE,"E62"),sQuery(id+"F2.wireOp",EDGE,"E65.0"),sQuery(id+"F2.wireOp",EDGE,"E70.MirrorCS")])]}),"instanceName":"3"});
            var Q33;
            Q33=makeQuery(id+"F4.opPattern","COPY",EDGE,{"derivedFrom":makeQuery(id+"F3.opExtrude","SWEPT_EDGE",EDGE,{"disambiguationData":[OSD([sQuery(id+"F0.wireOp",EDGE,"E62"),sQuery(id+"F2.wireOp",EDGE,"E65.0"),sQuery(id+"F2.wireOp",EDGE,"E70.MirrorCS")])]}),"instanceName":"4"});
            var Q34;
            Q34=makeQuery(id+"F4.opPattern","COPY",EDGE,{"derivedFrom":makeQuery(id+"F3.opExtrude","SWEPT_EDGE",EDGE,{"disambiguationData":[OSD([sQuery(id+"F0.wireOp",EDGE,"E62"),sQuery(id+"F2.wireOp",EDGE,"E65.0"),sQuery(id+"F2.wireOp",EDGE,"E70.MirrorCS")])]}),"instanceName":"5"});
            var Q35;
            Q35=makeQuery(id+"F4.opPattern","COPY",EDGE,{"derivedFrom":makeQuery(id+"F3.opExtrude","SWEPT_EDGE",EDGE,{"disambiguationData":[OSD([sQuery(id+"F0.wireOp",EDGE,"E62"),sQuery(id+"F2.wireOp",EDGE,"E65.0"),sQuery(id+"F2.wireOp",EDGE,"E70.MirrorCS")])]}),"instanceName":"6"});
            var Q36;
            Q36=makeQuery(id+"F4.opPattern","COPY",EDGE,{"derivedFrom":makeQuery(id+"F3.opExtrude","SWEPT_EDGE",EDGE,{"disambiguationData":[OSD([sQuery(id+"F0.wireOp",EDGE,"E62"),sQuery(id+"F2.wireOp",EDGE,"E65.0"),sQuery(id+"F2.wireOp",EDGE,"E70.MirrorCS")])]}),"instanceName":"7"});
            var Q37;
            Q37=makeQuery(id+"F4.opPattern","COPY",EDGE,{"derivedFrom":makeQuery(id+"F3.opExtrude","SWEPT_EDGE",EDGE,{"disambiguationData":[OSD([sQuery(id+"F0.wireOp",EDGE,"E62"),sQuery(id+"F2.wireOp",EDGE,"E65.0"),sQuery(id+"F2.wireOp",EDGE,"E70.MirrorCS")])]}),"instanceName":"8"});
            var Q38;
            Q38=makeQuery(id+"F4.opPattern","COPY",EDGE,{"derivedFrom":makeQuery(id+"F3.opExtrude","SWEPT_EDGE",EDGE,{"disambiguationData":[OSD([sQuery(id+"F0.wireOp",EDGE,"E62"),sQuery(id+"F2.wireOp",EDGE,"E65.0"),sQuery(id+"F2.wireOp",EDGE,"E70.MirrorCS")])]}),"instanceName":"9"});
            var Q39;
            Q39=makeQuery(id+"F4.opPattern","COPY",EDGE,{"derivedFrom":makeQuery(id+"F3.opExtrude","SWEPT_EDGE",EDGE,{"disambiguationData":[OSD([sQuery(id+"F0.wireOp",EDGE,"E62"),sQuery(id+"F2.wireOp",EDGE,"E65.0"),sQuery(id+"F2.wireOp",EDGE,"E70.MirrorCS")])]}),"instanceName":"10"});
            var Q40;
            Q40=makeQuery(id+"F4.opPattern","COPY",EDGE,{"derivedFrom":makeQuery(id+"F3.opExtrude","SWEPT_EDGE",EDGE,{"disambiguationData":[OSD([sQuery(id+"F0.wireOp",EDGE,"E62"),sQuery(id+"F2.wireOp",EDGE,"E65.0"),sQuery(id+"F2.wireOp",EDGE,"E70.MirrorCS")])]}),"instanceName":"11"});
            var Q41;
            Q41=makeQuery(id+"F4.opPattern","COPY",EDGE,{"derivedFrom":makeQuery(id+"F3.opExtrude","SWEPT_EDGE",EDGE,{"disambiguationData":[OSD([sQuery(id+"F0.wireOp",EDGE,"E62"),sQuery(id+"F2.wireOp",EDGE,"E65.0"),sQuery(id+"F2.wireOp",EDGE,"E70.MirrorCS")])]}),"instanceName":"12"});
            var Q42;
            Q42=makeQuery(id+"F4.opPattern","COPY",EDGE,{"derivedFrom":makeQuery(id+"F3.opExtrude","SWEPT_EDGE",EDGE,{"disambiguationData":[OSD([sQuery(id+"F0.wireOp",EDGE,"E62"),sQuery(id+"F2.wireOp",EDGE,"E65.0"),sQuery(id+"F2.wireOp",EDGE,"E70.MirrorCS")])]}),"instanceName":"13"});
            var Q43;
            Q43=makeQuery(id+"F4.opPattern","COPY",EDGE,{"derivedFrom":makeQuery(id+"F3.opExtrude","SWEPT_EDGE",EDGE,{"disambiguationData":[OSD([sQuery(id+"F0.wireOp",EDGE,"E62"),sQuery(id+"F2.wireOp",EDGE,"E65.0"),sQuery(id+"F2.wireOp",EDGE,"E70.MirrorCS")])]}),"instanceName":"14"});
            var Q44;
            Q44=makeQuery(id+"F4.opPattern","COPY",EDGE,{"derivedFrom":makeQuery(id+"F3.opExtrude","SWEPT_EDGE",EDGE,{"disambiguationData":[OSD([sQuery(id+"F0.wireOp",EDGE,"E62"),sQuery(id+"F2.wireOp",EDGE,"E65.0"),sQuery(id+"F2.wireOp",EDGE,"E70.MirrorCS")])]}),"instanceName":"15"});
            var Q45;
            Q45=makeQuery(id+"F4.opPattern","COPY",EDGE,{"derivedFrom":makeQuery(id+"F3.opExtrude","SWEPT_EDGE",EDGE,{"disambiguationData":[OSD([sQuery(id+"F0.wireOp",EDGE,"E62"),sQuery(id+"F2.wireOp",EDGE,"E65.0"),sQuery(id+"F2.wireOp",EDGE,"E70.MirrorCS")])]}),"instanceName":"16"});
            var Q46;
            Q46=makeQuery(id+"F4.opPattern","COPY",EDGE,{"derivedFrom":makeQuery(id+"F3.opExtrude","SWEPT_EDGE",EDGE,{"disambiguationData":[OSD([sQuery(id+"F0.wireOp",EDGE,"E62"),sQuery(id+"F2.wireOp",EDGE,"E65.0"),sQuery(id+"F2.wireOp",EDGE,"E70.MirrorCS")])]}),"instanceName":"17"});
            var Q47;
            Q47=makeQuery(id+"F4.opPattern","COPY",EDGE,{"derivedFrom":makeQuery(id+"F3.opExtrude","SWEPT_EDGE",EDGE,{"disambiguationData":[OSD([sQuery(id+"F0.wireOp",EDGE,"E62"),sQuery(id+"F2.wireOp",EDGE,"E65.0"),sQuery(id+"F2.wireOp",EDGE,"E70.MirrorCS")])]}),"instanceName":"18"});
            var Q48;
            Q48=makeQuery(id+"F4.opPattern","COPY",EDGE,{"derivedFrom":makeQuery(id+"F3.opExtrude","SWEPT_EDGE",EDGE,{"disambiguationData":[OSD([sQuery(id+"F0.wireOp",EDGE,"E62"),sQuery(id+"F2.wireOp",EDGE,"E65.0"),sQuery(id+"F2.wireOp",EDGE,"E70.MirrorCS")])]}),"instanceName":"19"});
            var Q49;
            Q49=makeQuery(id+"F4.opPattern","COPY",EDGE,{"derivedFrom":makeQuery(id+"F3.opExtrude","SWEPT_EDGE",EDGE,{"disambiguationData":[OSD([sQuery(id+"F0.wireOp",EDGE,"E62"),sQuery(id+"F2.wireOp",EDGE,"E65.0"),sQuery(id+"F2.wireOp",EDGE,"E70.MirrorCS")])]}),"instanceName":"20"});
            var Q50;
            Q50=makeQuery(id+"F4.opPattern","COPY",EDGE,{"derivedFrom":makeQuery(id+"F3.opExtrude","SWEPT_EDGE",EDGE,{"disambiguationData":[OSD([sQuery(id+"F0.wireOp",EDGE,"E62"),sQuery(id+"F2.wireOp",EDGE,"E65.0"),sQuery(id+"F2.wireOp",EDGE,"E70.MirrorCS")])]}),"instanceName":"21"});
            var Q51;
            Q51=makeQuery(id+"F4.opPattern","COPY",EDGE,{"derivedFrom":makeQuery(id+"F3.opExtrude","SWEPT_EDGE",EDGE,{"disambiguationData":[OSD([sQuery(id+"F0.wireOp",EDGE,"E62"),sQuery(id+"F2.wireOp",EDGE,"E65.0"),sQuery(id+"F2.wireOp",EDGE,"E70.MirrorCS")])]}),"instanceName":"22"});
            var Q52;
            Q52=makeQuery(id+"F4.opPattern","COPY",EDGE,{"derivedFrom":makeQuery(id+"F3.opExtrude","SWEPT_EDGE",EDGE,{"disambiguationData":[OSD([sQuery(id+"F0.wireOp",EDGE,"E62"),sQuery(id+"F2.wireOp",EDGE,"E65.0"),sQuery(id+"F2.wireOp",EDGE,"E70.MirrorCS")])]}),"instanceName":"23"});
            var Q53;
            Q53=makeQuery(id+"F4.opPattern","COPY",EDGE,{"derivedFrom":makeQuery(id+"F3.opExtrude","SWEPT_EDGE",EDGE,{"disambiguationData":[OSD([sQuery(id+"F0.wireOp",EDGE,"E62"),sQuery(id+"F2.wireOp",EDGE,"E65.0"),sQuery(id+"F2.wireOp",EDGE,"E70.MirrorCS")])]}),"instanceName":"24"});
            var Q54;
            Q54=makeQuery(id+"F4.opPattern","COPY",EDGE,{"derivedFrom":makeQuery(id+"F3.opExtrude","SWEPT_EDGE",EDGE,{"disambiguationData":[OSD([sQuery(id+"F0.wireOp",EDGE,"E62"),sQuery(id+"F2.wireOp",EDGE,"E65.0"),sQuery(id+"F2.wireOp",EDGE,"E70.MirrorCS")])]}),"instanceName":"25"});
            var Q55;
            Q55=makeQuery(id+"F4.opPattern","COPY",EDGE,{"derivedFrom":makeQuery(id+"F3.opExtrude","SWEPT_EDGE",EDGE,{"disambiguationData":[OSD([sQuery(id+"F0.wireOp",EDGE,"E62"),sQuery(id+"F2.wireOp",EDGE,"E65.0"),sQuery(id+"F2.wireOp",EDGE,"E70.MirrorCS")])]}),"instanceName":"26"});
            var Q56;
            Q56=makeQuery(id+"F4.opPattern","COPY",EDGE,{"derivedFrom":makeQuery(id+"F3.opExtrude","SWEPT_EDGE",EDGE,{"disambiguationData":[OSD([sQuery(id+"F0.wireOp",EDGE,"E62"),sQuery(id+"F2.wireOp",EDGE,"E65.0"),sQuery(id+"F2.wireOp",EDGE,"E70.MirrorCS")])]}),"instanceName":"27"});
            var Q57;
            Q57=makeQuery(id+"F4.opPattern","COPY",EDGE,{"derivedFrom":makeQuery(id+"F3.opExtrude","SWEPT_EDGE",EDGE,{"disambiguationData":[OSD([sQuery(id+"F0.wireOp",EDGE,"E62"),sQuery(id+"F2.wireOp",EDGE,"E65.0"),sQuery(id+"F2.wireOp",EDGE,"E70.MirrorCS")])]}),"instanceName":"28"});
            var Q58;
            Q58=makeQuery(id+"F4.opPattern","COPY",EDGE,{"derivedFrom":makeQuery(id+"F3.opExtrude","SWEPT_EDGE",EDGE,{"disambiguationData":[OSD([sQuery(id+"F0.wireOp",EDGE,"E62"),sQuery(id+"F2.wireOp",EDGE,"E65.0"),sQuery(id+"F2.wireOp",EDGE,"E66")])]}),"instanceName":"23"});
            var Q59;
            Q59=makeQuery(id+"F4.opPattern","COPY",EDGE,{"derivedFrom":makeQuery(id+"F3.opExtrude","SWEPT_EDGE",EDGE,{"disambiguationData":[OSD([sQuery(id+"F0.wireOp",EDGE,"E62"),sQuery(id+"F2.wireOp",EDGE,"E65.0"),sQuery(id+"F2.wireOp",EDGE,"E66")])]}),"instanceName":"25"});
            fillet(context, id + "F5", {"entities" : qUnion([Q0, Q1, Q2, Q3, Q4, Q5, Q6, Q7, Q8, Q9, Q10, Q11, Q12, Q13, Q14, Q15, Q16, Q17, Q18, Q19, Q20, Q21, Q22, Q23, Q24, Q25, Q26, Q27, Q28, Q29, Q30, Q31, Q32, Q33, Q34, Q35, Q36, Q37, Q38, Q39, Q40, Q41, Q42, Q43, Q44, Q45, Q46, Q47, Q48, Q49, Q50, Q51, Q52, Q53, Q54, Q55, Q56, Q57, Q58, Q59]), "radius" : 1.59 * mm, "tangentPropagation" : true, "allowEdgeOverflow" : false});
        }
    });
